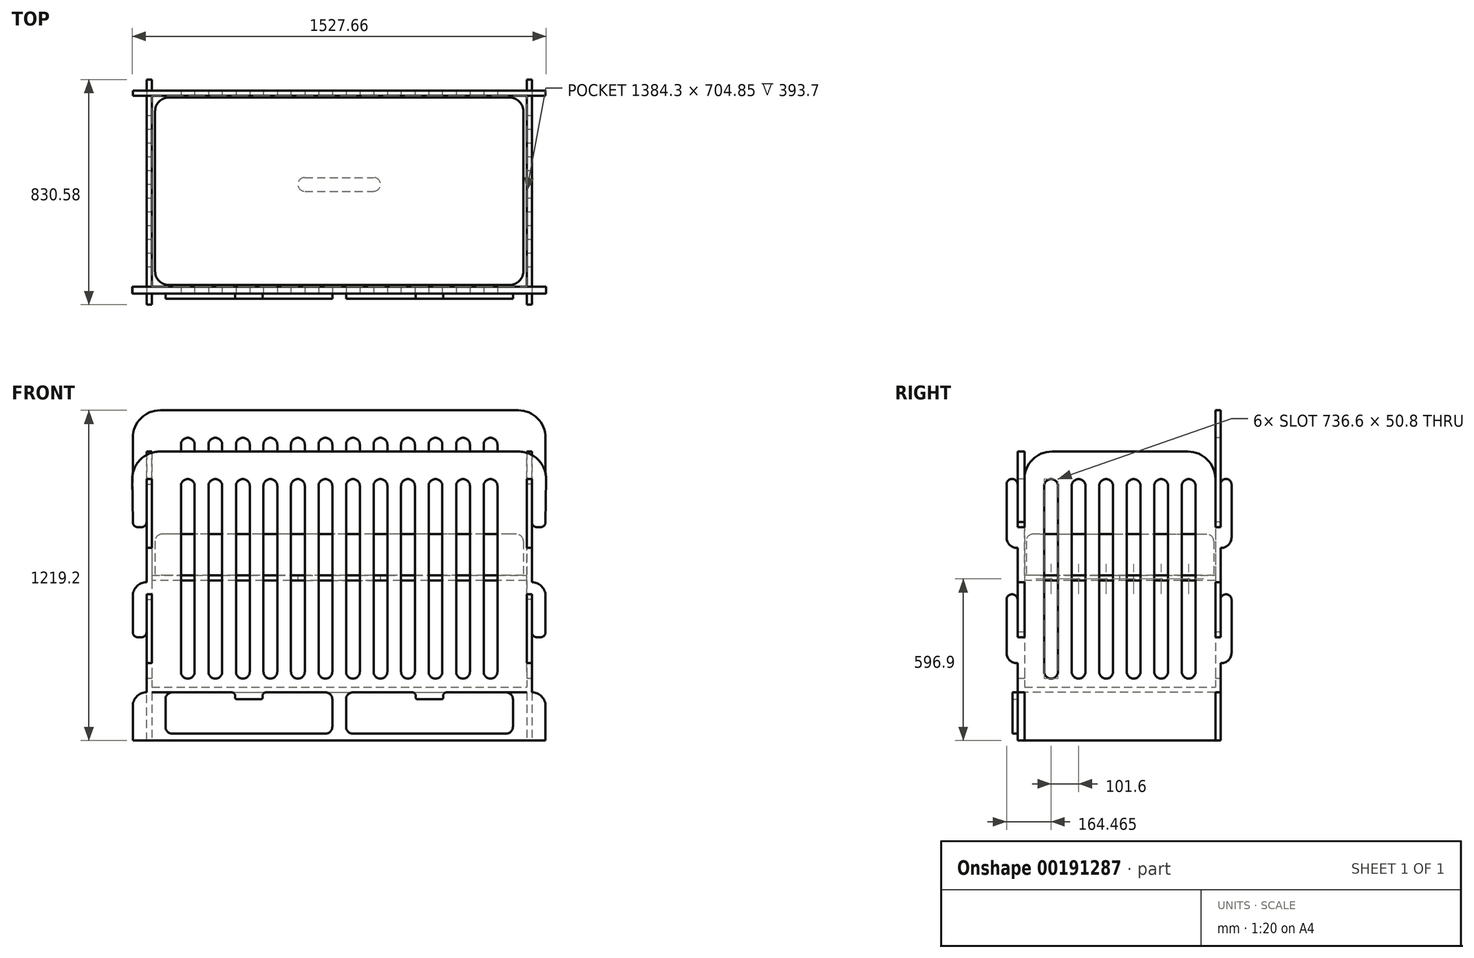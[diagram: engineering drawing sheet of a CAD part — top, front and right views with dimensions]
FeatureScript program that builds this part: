
annotation { "Feature Type Name" : "Feature", "Feature Type Description" : "" }
export const myFeature = defineFeature(function(context is Context, id is Id, definition is map)
    precondition{}
    {
        {
            var Q0;
            Q0=qCreatedBy(makeId("Front.planeOp"),FACE);
            var sketch = newSketch(context, id + "F0", { "sketchPlane" : qUnion([Q0])});
            skLineSegment(sketch, "E0", {"start": v(0, 360.7) * mm, "end": v(0, -747.32) * mm, "construction": true});
            skLineSegment(sketch, "E1", {"start": v(-1058.75, 0) * mm, "end": v(1231.14, 0) * mm, "construction": true});
            skLineSegment(sketch, "E2.bottom", {"start": v(-660.4, 304.8) * mm, "end": v(660.4, 304.8) * mm});
            skLineSegment(sketch, "E2.top", {"start": v(-762, -914.4) * mm, "end": v(762, -914.4) * mm});
            skLineSegment(sketch, "E2.left", {"start": v(-762, 203.2) * mm, "end": v(-762, -914.4) * mm});
            skLineSegment(sketch, "E2.right", {"start": v(762, 203.2) * mm, "end": v(762, -914.4) * mm});
            skPoint(sketch, "E3.visualSharp", {"position": v(-762, 304.8) * mm});
            skArc(sketch, "E3.filletArc", {"start": v(-660.4, 304.8) * mm, "mid": v(-732.24, 275.04) * mm, "end": v(-762, 203.2) * mm});
            skPoint(sketch, "E4.visualSharp", {"position": v(762, 304.8) * mm});
            skArc(sketch, "E4.filletArc", {"start": v(762, 203.2) * mm, "mid": v(732.24, 275.04) * mm, "end": v(660.4, 304.8) * mm});
            skSolve(sketch);
        }
        {
            var Q0;
            Q0 = qSketchRegion(id + "F0", true);
            extrude(context, id + "F1", {"entities" : qUnion([Q0]), "depth" : 19.05 * mm});
        }
        {
            var Q0;
            Q0=makeQuery(id+"F1.opExtrude","CAP_FACE",FACE,{"disambiguationData":[OSD([sQuery(id+"F0.wireOp",EDGE,"E2.bottom"),sQuery(id+"F0.wireOp",EDGE,"E2.top"),sQuery(id+"F0.wireOp",EDGE,"E2.left"),sQuery(id+"F0.wireOp",EDGE,"E2.right"),sQuery(id+"F0.wireOp",EDGE,"E3.filletArc"),sQuery(id+"F0.wireOp",EDGE,"E4.filletArc")])],"isStart":false});
            var sketch = newSketch(context, id + "F2", { "sketchPlane" : qUnion([Q0])});
            skLineSegment(sketch, "E5", {"start": v(-1021.81, 0) * mm, "end": v(1180, 0) * mm, "construction": true});
            skLineSegment(sketch, "E6", {"start": v(0, 448.77) * mm, "end": v(0, -914.4) * mm, "construction": true});
            skLineSegment(sketch, "E7", {"start": v(-742.95, -127) * mm, "end": v(-730.25, -127) * mm});
            skLineSegment(sketch, "E8", {"start": v(-711.2, -107.95) * mm, "end": v(-711.2, -50.8) * mm});
            skLineSegment(sketch, "E9", {"start": v(-711.2, -50.8) * mm, "end": v(-692.15, -50.8) * mm});
            skLineSegment(sketch, "E10", {"start": v(-692.15, -50.8) * mm, "end": v(-692.15, -330.2) * mm});
            skLineSegment(sketch, "E11", {"start": v(-762, -50.8) * mm, "end": v(-762, -107.95) * mm});
            skArc(sketch, "E12.filletArc", {"start": v(-762, -107.95) * mm, "mid": v(-756.42, -121.42) * mm, "end": v(-742.95, -127) * mm});
            skPoint(sketch, "E13.visualSharp", {"position": v(-762, -330.2) * mm});
            skPoint(sketch, "E14.visualSharp", {"position": v(-711.2, -127) * mm});
            skArc(sketch, "E14.filletArc", {"start": v(-730.25, -127) * mm, "mid": v(-716.78, -121.42) * mm, "end": v(-711.2, -107.95) * mm});
            skLineSegment(sketch, "E15", {"start": v(-762, -50.8) * mm, "end": v(-838.2, -50.8) * mm});
            skLineSegment(sketch, "E16", {"start": v(-838.2, -50.8) * mm, "end": v(-838.2, -431.8) * mm});
            skLineSegment(sketch, "E17", {"start": v(-838.2, -431.8) * mm, "end": v(-762, -431.8) * mm});
            skLineSegment(sketch, "E18", {"start": v(-692.15, -330.2) * mm, "end": v(-711.2, -330.2) * mm});
            skLineSegment(sketch, "E19", {"start": v(-762, -381) * mm, "end": v(-762, -431.8) * mm});
            skArc(sketch, "E20.filletArc", {"start": v(-711.2, -330.2) * mm, "mid": v(-747.12, -345.08) * mm, "end": v(-762, -381) * mm});
            skLineSegment(sketch, "E21.0.1.0", {"start": v(-711.2, -514.35) * mm, "end": v(-711.2, -457.2) * mm});
            skLineSegment(sketch, "E21.0.1.1", {"start": v(-838.2, -838.2) * mm, "end": v(-762, -838.2) * mm});
            skPoint(sketch, "E21.0.1.2", {"position": v(-762, -736.6) * mm});
            skArc(sketch, "E21.0.1.3", {"start": v(-711.2, -736.6) * mm, "mid": v(-747.12, -751.48) * mm, "end": v(-762, -787.4) * mm});
            skLineSegment(sketch, "E21.0.1.4", {"start": v(-762, -457.2) * mm, "end": v(-838.2, -457.2) * mm});
            skLineSegment(sketch, "E21.0.1.5", {"start": v(-762, -787.4) * mm, "end": v(-762, -838.2) * mm});
            skLineSegment(sketch, "E21.0.1.6", {"start": v(-692.15, -457.2) * mm, "end": v(-692.15, -736.6) * mm});
            skLineSegment(sketch, "E21.0.1.7", {"start": v(-838.2, -457.2) * mm, "end": v(-838.2, -838.2) * mm});
            skLineSegment(sketch, "E21.0.1.8", {"start": v(-762, -457.2) * mm, "end": v(-762, -514.35) * mm});
            skPoint(sketch, "E21.0.1.9", {"position": v(-711.2, -533.4) * mm});
            skPoint(sketch, "E21.0.1.10", {"position": v(-762, -736.6) * mm});
            skLineSegment(sketch, "E21.0.1.11", {"start": v(-711.2, -457.2) * mm, "end": v(-692.15, -457.2) * mm});
            skArc(sketch, "E21.0.1.12", {"start": v(-762, -514.35) * mm, "mid": v(-756.42, -527.82) * mm, "end": v(-742.95, -533.4) * mm});
            skLineSegment(sketch, "E21.0.1.13", {"start": v(-742.95, -533.4) * mm, "end": v(-730.25, -533.4) * mm});
            skLineSegment(sketch, "E21.0.1.14", {"start": v(-692.15, -736.6) * mm, "end": v(-711.2, -736.6) * mm});
            skArc(sketch, "E21.0.1.15", {"start": v(-730.25, -533.4) * mm, "mid": v(-716.78, -527.82) * mm, "end": v(-711.2, -514.35) * mm});
            skLineSegment(sketch, "E21.direction1", {"start": v(-838.2, -431.8) * mm, "end": v(-812.8, -431.8) * mm, "construction": true});
            skLineSegment(sketch, "E21.direction2", {"start": v(-838.2, -431.8) * mm, "end": v(-838.2, -838.2) * mm, "construction": true});
            skLineSegment(sketch, "E22.MirrorCS", {"start": v(742.95, -127) * mm, "end": v(730.25, -127) * mm});
            skLineSegment(sketch, "E23.MirrorCS", {"start": v(692.15, -330.2) * mm, "end": v(711.2, -330.2) * mm});
            skArc(sketch, "E24.MirrorCS", {"start": v(762, -107.95) * mm, "mid": v(756.42, -121.42) * mm, "end": v(742.95, -127) * mm});
            skLineSegment(sketch, "E25.MirrorCS", {"start": v(692.15, -736.6) * mm, "end": v(711.2, -736.6) * mm});
            skLineSegment(sketch, "E26.MirrorCS", {"start": v(711.2, -50.8) * mm, "end": v(692.15, -50.8) * mm});
            skArc(sketch, "E27.MirrorCS", {"start": v(730.25, -127) * mm, "mid": v(716.78, -121.42) * mm, "end": v(711.2, -107.95) * mm});
            skLineSegment(sketch, "E28.MirrorCS", {"start": v(742.95, -533.4) * mm, "end": v(730.25, -533.4) * mm});
            skArc(sketch, "E29.MirrorCS", {"start": v(762, -514.35) * mm, "mid": v(756.42, -527.82) * mm, "end": v(742.95, -533.4) * mm});
            skLineSegment(sketch, "E30.MirrorCS", {"start": v(711.2, -457.2) * mm, "end": v(692.15, -457.2) * mm});
            skArc(sketch, "E31.MirrorCS", {"start": v(730.25, -533.4) * mm, "mid": v(716.78, -527.82) * mm, "end": v(711.2, -514.35) * mm});
            skLineSegment(sketch, "E32.MirrorCS", {"start": v(838.2, -457.2) * mm, "end": v(838.2, -838.2) * mm});
            skLineSegment(sketch, "E33.MirrorCS", {"start": v(838.2, -431.8) * mm, "end": v(838.2, -838.2) * mm, "construction": true});
            skLineSegment(sketch, "E34.MirrorCS", {"start": v(838.2, -431.8) * mm, "end": v(812.8, -431.8) * mm, "construction": true});
            skPoint(sketch, "E35.MirrorP", {"position": v(762, -736.6) * mm});
            skPoint(sketch, "E36.MirrorP", {"position": v(762, -330.2) * mm});
            skLineSegment(sketch, "E37.MirrorCS", {"start": v(711.2, -107.95) * mm, "end": v(711.2, -50.8) * mm});
            skLineSegment(sketch, "E38.MirrorCS", {"start": v(692.15, -50.8) * mm, "end": v(692.15, -330.2) * mm});
            skLineSegment(sketch, "E39.MirrorCS", {"start": v(762, -50.8) * mm, "end": v(762, -107.95) * mm});
            skLineSegment(sketch, "E40.MirrorCS", {"start": v(762, -787.4) * mm, "end": v(762, -838.2) * mm});
            skLineSegment(sketch, "E41.MirrorCS", {"start": v(762, -457.2) * mm, "end": v(838.2, -457.2) * mm});
            skPoint(sketch, "E42.MirrorP", {"position": v(711.2, -533.4) * mm});
            skLineSegment(sketch, "E43.MirrorCS", {"start": v(838.2, -431.8) * mm, "end": v(762, -431.8) * mm});
            skLineSegment(sketch, "E44.MirrorCS", {"start": v(762, -50.8) * mm, "end": v(838.2, -50.8) * mm});
            skLineSegment(sketch, "E45.MirrorCS", {"start": v(762, -457.2) * mm, "end": v(762, -514.35) * mm});
            skLineSegment(sketch, "E46.MirrorCS", {"start": v(838.2, -50.8) * mm, "end": v(838.2, -431.8) * mm});
            skLineSegment(sketch, "E47.MirrorCS", {"start": v(711.2, -514.35) * mm, "end": v(711.2, -457.2) * mm});
            skArc(sketch, "E48.MirrorCS", {"start": v(711.2, -330.2) * mm, "mid": v(747.12, -345.08) * mm, "end": v(762, -381) * mm});
            skLineSegment(sketch, "E49.MirrorCS", {"start": v(762, -381) * mm, "end": v(762, -431.8) * mm});
            skArc(sketch, "E50.MirrorCS", {"start": v(711.2, -736.6) * mm, "mid": v(747.12, -751.48) * mm, "end": v(762, -787.4) * mm});
            skPoint(sketch, "E51.MirrorP", {"position": v(711.2, -127) * mm});
            skLineSegment(sketch, "E52.MirrorCS", {"start": v(838.2, -838.2) * mm, "end": v(762, -838.2) * mm});
            skLineSegment(sketch, "E53.MirrorCS", {"start": v(692.15, -457.2) * mm, "end": v(692.15, -736.6) * mm});
            skSolve(sketch);
        }
        {
            var Q0;
            Q0 = qSketchRegion(id + "F2", true);
            extrude(context, id + "F3", {"entities" : qUnion([Q0]), "operationType" : NewBodyOperationType.REMOVE, "endBound" : BoundingType.THROUGH_ALL, "oppositeDirection" : true, "depth" : 25.4 * mm});
        }
        {
            var Q0;
            Q0=makeQuery(id+"F1.opExtrude","CAP_FACE",FACE,{"disambiguationData":[OSD([sQuery(id+"F0.wireOp",EDGE,"E2.bottom"),sQuery(id+"F0.wireOp",EDGE,"E2.top"),sQuery(id+"F0.wireOp",EDGE,"E2.left"),sQuery(id+"F0.wireOp",EDGE,"E2.right"),sQuery(id+"F0.wireOp",EDGE,"E3.filletArc"),sQuery(id+"F0.wireOp",EDGE,"E4.filletArc")])],"isStart":false});
            var sketch = newSketch(context, id + "F4", { "sketchPlane" : qUnion([Q0])});
            skLineSegment(sketch, "E54", {"start": v(0, 304.8) * mm, "end": v(0, -914.4) * mm, "construction": true});
            skLineSegment(sketch, "E55", {"start": v(-762, 0) * mm, "end": v(762, 0) * mm, "construction": true});
            skLineSegment(sketch, "E56.bottom", {"start": v(-50.8, 203.2) * mm, "end": v(-50.8, 203.2) * mm});
            skLineSegment(sketch, "E56.top", {"start": v(-50.8, -685.8) * mm, "end": v(-50.8, -685.8) * mm});
            skLineSegment(sketch, "E56.left", {"start": v(-76.2, 177.8) * mm, "end": v(-76.2, -660.4) * mm});
            skLineSegment(sketch, "E56.right", {"start": v(-25.4, 177.8) * mm, "end": v(-25.4, -660.4) * mm});
            skLineSegment(sketch, "E57", {"start": v(-762, -787.4) * mm, "end": v(762, -787.4) * mm, "construction": true});
            skPoint(sketch, "E58.visualSharp", {"position": v(-76.2, 203.2) * mm});
            skArc(sketch, "E58.filletArc", {"start": v(-50.8, 203.2) * mm, "mid": v(-68.76, 195.76) * mm, "end": v(-76.2, 177.8) * mm});
            skPoint(sketch, "E59.visualSharp", {"position": v(-25.4, 203.2) * mm});
            skArc(sketch, "E59.filletArc", {"start": v(-25.4, 177.8) * mm, "mid": v(-32.84, 195.76) * mm, "end": v(-50.8, 203.2) * mm});
            skPoint(sketch, "E60.visualSharp", {"position": v(-76.2, -685.8) * mm});
            skArc(sketch, "E60.filletArc", {"start": v(-76.2, -660.4) * mm, "mid": v(-68.76, -678.36) * mm, "end": v(-50.8, -685.8) * mm});
            skPoint(sketch, "E61.visualSharp", {"position": v(-25.4, -685.8) * mm});
            skArc(sketch, "E61.filletArc", {"start": v(-50.8, -685.8) * mm, "mid": v(-32.84, -678.36) * mm, "end": v(-25.4, -660.4) * mm});
            skLineSegment(sketch, "E62.1.0.0", {"start": v(-177.8, 177.8) * mm, "end": v(-177.8, -660.4) * mm});
            skLineSegment(sketch, "E62.1.0.1", {"start": v(-127, 177.8) * mm, "end": v(-127, -660.4) * mm});
            skPoint(sketch, "E62.1.0.2", {"position": v(-127, -685.8) * mm});
            skPoint(sketch, "E62.1.0.3", {"position": v(-177.8, -685.8) * mm});
            skPoint(sketch, "E62.1.0.4", {"position": v(-127, 203.2) * mm});
            skPoint(sketch, "E62.1.0.5", {"position": v(-177.8, 203.2) * mm});
            skArc(sketch, "E62.1.0.6", {"start": v(-127, 177.8) * mm, "mid": v(-134.44, 195.76) * mm, "end": v(-152.4, 203.2) * mm});
            skArc(sketch, "E62.1.0.7", {"start": v(-177.8, -660.4) * mm, "mid": v(-170.36, -678.36) * mm, "end": v(-152.4, -685.8) * mm});
            skArc(sketch, "E62.1.0.8", {"start": v(-152.4, -685.8) * mm, "mid": v(-134.44, -678.36) * mm, "end": v(-127, -660.4) * mm});
            skArc(sketch, "E62.1.0.9", {"start": v(-152.4, 203.2) * mm, "mid": v(-170.36, 195.76) * mm, "end": v(-177.8, 177.8) * mm});
            skLineSegment(sketch, "E62.2.0.0", {"start": v(-279.4, 177.8) * mm, "end": v(-279.4, -660.4) * mm});
            skLineSegment(sketch, "E62.2.0.1", {"start": v(-228.6, 177.8) * mm, "end": v(-228.6, -660.4) * mm});
            skPoint(sketch, "E62.2.0.2", {"position": v(-228.6, -685.8) * mm});
            skPoint(sketch, "E62.2.0.3", {"position": v(-279.4, -685.8) * mm});
            skPoint(sketch, "E62.2.0.4", {"position": v(-228.6, 203.2) * mm});
            skPoint(sketch, "E62.2.0.5", {"position": v(-279.4, 203.2) * mm});
            skArc(sketch, "E62.2.0.6", {"start": v(-228.6, 177.8) * mm, "mid": v(-236.04, 195.76) * mm, "end": v(-254, 203.2) * mm});
            skArc(sketch, "E62.2.0.7", {"start": v(-279.4, -660.4) * mm, "mid": v(-271.96, -678.36) * mm, "end": v(-254, -685.8) * mm});
            skArc(sketch, "E62.2.0.8", {"start": v(-254, -685.8) * mm, "mid": v(-236.04, -678.36) * mm, "end": v(-228.6, -660.4) * mm});
            skArc(sketch, "E62.2.0.9", {"start": v(-254, 203.2) * mm, "mid": v(-271.96, 195.76) * mm, "end": v(-279.4, 177.8) * mm});
            skLineSegment(sketch, "E62.3.0.0", {"start": v(-381, 177.8) * mm, "end": v(-381, -660.4) * mm});
            skLineSegment(sketch, "E62.3.0.1", {"start": v(-330.2, 177.8) * mm, "end": v(-330.2, -660.4) * mm});
            skPoint(sketch, "E62.3.0.2", {"position": v(-330.2, -685.8) * mm});
            skPoint(sketch, "E62.3.0.3", {"position": v(-381, -685.8) * mm});
            skPoint(sketch, "E62.3.0.4", {"position": v(-330.2, 203.2) * mm});
            skPoint(sketch, "E62.3.0.5", {"position": v(-381, 203.2) * mm});
            skArc(sketch, "E62.3.0.6", {"start": v(-330.2, 177.8) * mm, "mid": v(-337.64, 195.76) * mm, "end": v(-355.6, 203.2) * mm});
            skArc(sketch, "E62.3.0.7", {"start": v(-381, -660.4) * mm, "mid": v(-373.56, -678.36) * mm, "end": v(-355.6, -685.8) * mm});
            skArc(sketch, "E62.3.0.8", {"start": v(-355.6, -685.8) * mm, "mid": v(-337.64, -678.36) * mm, "end": v(-330.2, -660.4) * mm});
            skArc(sketch, "E62.3.0.9", {"start": v(-355.6, 203.2) * mm, "mid": v(-373.56, 195.76) * mm, "end": v(-381, 177.8) * mm});
            skLineSegment(sketch, "E62.4.0.0", {"start": v(-482.6, 177.8) * mm, "end": v(-482.6, -660.4) * mm});
            skLineSegment(sketch, "E62.4.0.1", {"start": v(-431.8, 177.8) * mm, "end": v(-431.8, -660.4) * mm});
            skPoint(sketch, "E62.4.0.2", {"position": v(-431.8, -685.8) * mm});
            skPoint(sketch, "E62.4.0.3", {"position": v(-482.6, -685.8) * mm});
            skPoint(sketch, "E62.4.0.4", {"position": v(-431.8, 203.2) * mm});
            skPoint(sketch, "E62.4.0.5", {"position": v(-482.6, 203.2) * mm});
            skArc(sketch, "E62.4.0.6", {"start": v(-431.8, 177.8) * mm, "mid": v(-439.24, 195.76) * mm, "end": v(-457.2, 203.2) * mm});
            skArc(sketch, "E62.4.0.7", {"start": v(-482.6, -660.4) * mm, "mid": v(-475.16, -678.36) * mm, "end": v(-457.2, -685.8) * mm});
            skArc(sketch, "E62.4.0.8", {"start": v(-457.2, -685.8) * mm, "mid": v(-439.24, -678.36) * mm, "end": v(-431.8, -660.4) * mm});
            skArc(sketch, "E62.4.0.9", {"start": v(-457.2, 203.2) * mm, "mid": v(-475.16, 195.76) * mm, "end": v(-482.6, 177.8) * mm});
            skLineSegment(sketch, "E62.5.0.0", {"start": v(-584.2, 177.8) * mm, "end": v(-584.2, -660.4) * mm});
            skLineSegment(sketch, "E62.5.0.1", {"start": v(-533.4, 177.8) * mm, "end": v(-533.4, -660.4) * mm});
            skPoint(sketch, "E62.5.0.2", {"position": v(-533.4, -685.8) * mm});
            skPoint(sketch, "E62.5.0.3", {"position": v(-584.2, -685.8) * mm});
            skPoint(sketch, "E62.5.0.4", {"position": v(-533.4, 203.2) * mm});
            skPoint(sketch, "E62.5.0.5", {"position": v(-584.2, 203.2) * mm});
            skArc(sketch, "E62.5.0.6", {"start": v(-533.4, 177.8) * mm, "mid": v(-540.84, 195.76) * mm, "end": v(-558.8, 203.2) * mm});
            skArc(sketch, "E62.5.0.7", {"start": v(-584.2, -660.4) * mm, "mid": v(-576.76, -678.36) * mm, "end": v(-558.8, -685.8) * mm});
            skArc(sketch, "E62.5.0.8", {"start": v(-558.8, -685.8) * mm, "mid": v(-540.84, -678.36) * mm, "end": v(-533.4, -660.4) * mm});
            skArc(sketch, "E62.5.0.9", {"start": v(-558.8, 203.2) * mm, "mid": v(-576.76, 195.76) * mm, "end": v(-584.2, 177.8) * mm});
            skLineSegment(sketch, "E62.direction1", {"start": v(-76.2, -685.8) * mm, "end": v(-177.8, -685.8) * mm, "construction": true});
            skLineSegment(sketch, "E63.MirrorCS", {"start": v(76.2, -685.8) * mm, "end": v(177.8, -685.8) * mm, "construction": true});
            skArc(sketch, "E64.MirrorCS", {"start": v(152.4, -685.8) * mm, "mid": v(134.44, -678.36) * mm, "end": v(127, -660.4) * mm});
            skArc(sketch, "E65.MirrorCS", {"start": v(457.2, 203.2) * mm, "mid": v(475.16, 195.76) * mm, "end": v(482.6, 177.8) * mm});
            skArc(sketch, "E66.MirrorCS", {"start": v(152.4, 203.2) * mm, "mid": v(170.36, 195.76) * mm, "end": v(177.8, 177.8) * mm});
            skArc(sketch, "E67.MirrorCS", {"start": v(279.4, -660.4) * mm, "mid": v(271.96, -678.36) * mm, "end": v(254, -685.8) * mm});
            skArc(sketch, "E68.MirrorCS", {"start": v(431.8, 177.8) * mm, "mid": v(439.24, 195.76) * mm, "end": v(457.2, 203.2) * mm});
            skArc(sketch, "E69.MirrorCS", {"start": v(533.4, 177.8) * mm, "mid": v(540.84, 195.76) * mm, "end": v(558.8, 203.2) * mm});
            skArc(sketch, "E70.MirrorCS", {"start": v(254, -685.8) * mm, "mid": v(236.04, -678.36) * mm, "end": v(228.6, -660.4) * mm});
            skArc(sketch, "E71.MirrorCS", {"start": v(584.2, -660.4) * mm, "mid": v(576.76, -678.36) * mm, "end": v(558.8, -685.8) * mm});
            skArc(sketch, "E72.MirrorCS", {"start": v(254, 203.2) * mm, "mid": v(271.96, 195.76) * mm, "end": v(279.4, 177.8) * mm});
            skArc(sketch, "E73.MirrorCS", {"start": v(330.2, 177.8) * mm, "mid": v(337.64, 195.76) * mm, "end": v(355.6, 203.2) * mm});
            skArc(sketch, "E74.MirrorCS", {"start": v(482.6, -660.4) * mm, "mid": v(475.16, -678.36) * mm, "end": v(457.2, -685.8) * mm});
            skArc(sketch, "E75.MirrorCS", {"start": v(177.8, -660.4) * mm, "mid": v(170.36, -678.36) * mm, "end": v(152.4, -685.8) * mm});
            skArc(sketch, "E76.MirrorCS", {"start": v(381, -660.4) * mm, "mid": v(373.56, -678.36) * mm, "end": v(355.6, -685.8) * mm});
            skArc(sketch, "E77.MirrorCS", {"start": v(355.6, -685.8) * mm, "mid": v(337.64, -678.36) * mm, "end": v(330.2, -660.4) * mm});
            skArc(sketch, "E78.MirrorCS", {"start": v(127, 177.8) * mm, "mid": v(134.44, 195.76) * mm, "end": v(152.4, 203.2) * mm});
            skArc(sketch, "E79.MirrorCS", {"start": v(50.8, -685.8) * mm, "mid": v(32.84, -678.36) * mm, "end": v(25.4, -660.4) * mm});
            skArc(sketch, "E80.MirrorCS", {"start": v(457.2, -685.8) * mm, "mid": v(439.24, -678.36) * mm, "end": v(431.8, -660.4) * mm});
            skArc(sketch, "E81.MirrorCS", {"start": v(558.8, 203.2) * mm, "mid": v(576.76, 195.76) * mm, "end": v(584.2, 177.8) * mm});
            skArc(sketch, "E82.MirrorCS", {"start": v(558.8, -685.8) * mm, "mid": v(540.84, -678.36) * mm, "end": v(533.4, -660.4) * mm});
            skArc(sketch, "E83.MirrorCS", {"start": v(76.2, -660.4) * mm, "mid": v(68.76, -678.36) * mm, "end": v(50.8, -685.8) * mm});
            skArc(sketch, "E84.MirrorCS", {"start": v(25.4, 177.8) * mm, "mid": v(32.84, 195.76) * mm, "end": v(50.8, 203.2) * mm});
            skArc(sketch, "E85.MirrorCS", {"start": v(355.6, 203.2) * mm, "mid": v(373.56, 195.76) * mm, "end": v(381, 177.8) * mm});
            skArc(sketch, "E86.MirrorCS", {"start": v(228.6, 177.8) * mm, "mid": v(236.04, 195.76) * mm, "end": v(254, 203.2) * mm});
            skArc(sketch, "E87.MirrorCS", {"start": v(50.8, 203.2) * mm, "mid": v(68.76, 195.76) * mm, "end": v(76.2, 177.8) * mm});
            skPoint(sketch, "E88.MirrorP", {"position": v(76.2, 203.2) * mm});
            skPoint(sketch, "E89.MirrorP", {"position": v(381, 203.2) * mm});
            skPoint(sketch, "E90.MirrorP", {"position": v(177.8, 203.2) * mm});
            skLineSegment(sketch, "E91.MirrorCS", {"start": v(533.4, 177.8) * mm, "end": v(533.4, -660.4) * mm});
            skPoint(sketch, "E92.MirrorP", {"position": v(228.6, 203.2) * mm});
            skPoint(sketch, "E93.MirrorP", {"position": v(584.2, 203.2) * mm});
            skPoint(sketch, "E94.MirrorP", {"position": v(431.8, 203.2) * mm});
            skPoint(sketch, "E95.MirrorP", {"position": v(482.6, 203.2) * mm});
            skPoint(sketch, "E96.MirrorP", {"position": v(279.4, 203.2) * mm});
            skLineSegment(sketch, "E97.MirrorCS", {"start": v(482.6, 177.8) * mm, "end": v(482.6, -660.4) * mm});
            skPoint(sketch, "E98.MirrorP", {"position": v(76.2, -685.8) * mm});
            skLineSegment(sketch, "E99.MirrorCS", {"start": v(279.4, 177.8) * mm, "end": v(279.4, -660.4) * mm});
            skLineSegment(sketch, "E100.MirrorCS", {"start": v(228.6, 177.8) * mm, "end": v(228.6, -660.4) * mm});
            skLineSegment(sketch, "E101.MirrorCS", {"start": v(76.2, 177.8) * mm, "end": v(76.2, -660.4) * mm});
            skPoint(sketch, "E102.MirrorP", {"position": v(127, 203.2) * mm});
            skLineSegment(sketch, "E103.MirrorCS", {"start": v(25.4, 177.8) * mm, "end": v(25.4, -660.4) * mm});
            skPoint(sketch, "E104.MirrorP", {"position": v(25.4, -685.8) * mm});
            skPoint(sketch, "E105.MirrorP", {"position": v(533.4, -685.8) * mm});
            skLineSegment(sketch, "E106.MirrorCS", {"start": v(381, 177.8) * mm, "end": v(381, -660.4) * mm});
            skPoint(sketch, "E107.MirrorP", {"position": v(330.2, -685.8) * mm});
            skPoint(sketch, "E108.MirrorP", {"position": v(127, -685.8) * mm});
            skPoint(sketch, "E109.MirrorP", {"position": v(431.8, -685.8) * mm});
            skPoint(sketch, "E110.MirrorP", {"position": v(228.6, -685.8) * mm});
            skLineSegment(sketch, "E111.MirrorCS", {"start": v(431.8, 177.8) * mm, "end": v(431.8, -660.4) * mm});
            skPoint(sketch, "E112.MirrorP", {"position": v(381, -685.8) * mm});
            skPoint(sketch, "E113.MirrorP", {"position": v(177.8, -685.8) * mm});
            skLineSegment(sketch, "E114.MirrorCS", {"start": v(330.2, 177.8) * mm, "end": v(330.2, -660.4) * mm});
            skLineSegment(sketch, "E115.MirrorCS", {"start": v(127, 177.8) * mm, "end": v(127, -660.4) * mm});
            skPoint(sketch, "E116.MirrorP", {"position": v(25.4, 203.2) * mm});
            skLineSegment(sketch, "E117.MirrorCS", {"start": v(177.8, 177.8) * mm, "end": v(177.8, -660.4) * mm});
            skPoint(sketch, "E118.MirrorP", {"position": v(330.2, 203.2) * mm});
            skPoint(sketch, "E119.MirrorP", {"position": v(482.6, -685.8) * mm});
            skPoint(sketch, "E120.MirrorP", {"position": v(584.2, -685.8) * mm});
            skPoint(sketch, "E121.MirrorP", {"position": v(533.4, 203.2) * mm});
            skLineSegment(sketch, "E122.MirrorCS", {"start": v(584.2, 177.8) * mm, "end": v(584.2, -660.4) * mm});
            skPoint(sketch, "E123.MirrorP", {"position": v(279.4, -685.8) * mm});
            skSolve(sketch);
        }
        {
            var Q0;
            Q0 = qSketchRegion(id + "F4", true);
            extrude(context, id + "F5", {"entities" : qUnion([Q0]), "operationType" : NewBodyOperationType.REMOVE, "endBound" : BoundingType.THROUGH_ALL, "oppositeDirection" : true, "depth" : 25.4 * mm});
        }
        {
            var Q0;
            Q0=makeQuery(id+"F3.boolean.opBoolean","COPY",FACE,{"derivedFrom":makeQuery(id+"F3.opExtrude","SWEPT_FACE",FACE,{"disambiguationData":[OSD([sQuery(id+"F2.wireOp",EDGE,"E10")])]})});
            var sketch = newSketch(context, id + "F6", { "sketchPlane" : qUnion([Q0])});
            skPoint(sketch, "E124.0", {"position": v(0, -914.4) * mm});
            skLineSegment(sketch, "E125.bottom", {"start": v(0, -914.4) * mm, "end": v(749.3, -914.4) * mm});
            skLineSegment(sketch, "E125.top", {"start": v(0, 0) * mm, "end": v(749.3, 0) * mm});
            skLineSegment(sketch, "E126", {"start": v(0, 0) * mm, "end": v(0, 31.75) * mm});
            skLineSegment(sketch, "E127", {"start": v(-19.05, 50.8) * mm, "end": v(-21.6, 50.8) * mm});
            skLineSegment(sketch, "E128", {"start": v(-40.64, 31.75) * mm, "end": v(-40.64, -165.1) * mm});
            skLineSegment(sketch, "E129", {"start": v(-2.54, -203.2) * mm, "end": v(0, -203.2) * mm});
            skPoint(sketch, "E129.endSnap0", {"position": v(0, -190.5) * mm});
            skLineSegment(sketch, "E130.trimOffspring", {"start": v(0, -50.8) * mm, "end": v(0, 0) * mm});
            skPoint(sketch, "E131.0", {"position": v(0, -457.2) * mm});
            skLineSegment(sketch, "E132", {"start": v(0, -457.2) * mm, "end": v(0, -393.94) * mm});
            skLineSegment(sketch, "E133", {"start": v(-19.05, -374.9) * mm, "end": v(-21.6, -374.9) * mm});
            skLineSegment(sketch, "E134", {"start": v(-40.64, -393.94) * mm, "end": v(-40.64, -590.8) * mm});
            skLineSegment(sketch, "E135", {"start": v(-2.54, -628.9) * mm, "end": v(0, -628.9) * mm});
            skPoint(sketch, "E136.visualSharp", {"position": v(0, 50.8) * mm});
            skArc(sketch, "E136.filletArc", {"start": v(0, 31.75) * mm, "mid": v(-5.58, 45.22) * mm, "end": v(-19.05, 50.8) * mm});
            skPoint(sketch, "E137.visualSharp", {"position": v(-40.64, 50.8) * mm});
            skArc(sketch, "E137.filletArc", {"start": v(-21.6, 50.8) * mm, "mid": v(-35.06, 45.22) * mm, "end": v(-40.64, 31.75) * mm});
            skPoint(sketch, "E138.visualSharp", {"position": v(-40.64, -203.2) * mm});
            skArc(sketch, "E138.filletArc", {"start": v(-40.64, -165.1) * mm, "mid": v(-29.48, -192.04) * mm, "end": v(-2.54, -203.2) * mm});
            skArc(sketch, "E139.filletArc", {"start": v(0, -393.94) * mm, "mid": v(-5.58, -380.47) * mm, "end": v(-19.05, -374.9) * mm});
            skPoint(sketch, "E140.visualSharp", {"position": v(-40.64, -374.9) * mm});
            skArc(sketch, "E140.filletArc", {"start": v(-21.6, -374.9) * mm, "mid": v(-35.06, -380.47) * mm, "end": v(-40.64, -393.94) * mm});
            skLineSegment(sketch, "E141", {"start": v(0, -393.94) * mm, "end": v(0, -203.2) * mm});
            skPoint(sketch, "E142.visualSharp", {"position": v(-40.64, -628.9) * mm});
            skArc(sketch, "E142.filletArc", {"start": v(-40.64, -590.8) * mm, "mid": v(-29.48, -617.73) * mm, "end": v(-2.54, -628.9) * mm});
            skLineSegment(sketch, "E143", {"start": v(0, -914.4) * mm, "end": v(0, -628.9) * mm});
            skLineSegment(sketch, "E144", {"start": v(374.65, 0) * mm, "end": v(374.65, -914.4) * mm, "construction": true});
            skLineSegment(sketch, "E145.MirrorCS", {"start": v(751.84, -203.2) * mm, "end": v(749.3, -203.2) * mm});
            skLineSegment(sketch, "E146.MirrorCS", {"start": v(768.35, 50.8) * mm, "end": v(770.89, 50.8) * mm});
            skLineSegment(sketch, "E147.MirrorCS", {"start": v(749.3, 0) * mm, "end": v(749.3, 31.75) * mm});
            skArc(sketch, "E148.MirrorCS", {"start": v(770.89, 50.8) * mm, "mid": v(784.36, 45.22) * mm, "end": v(789.94, 31.75) * mm});
            skArc(sketch, "E149.MirrorCS", {"start": v(749.3, 31.75) * mm, "mid": v(754.88, 45.22) * mm, "end": v(768.35, 50.8) * mm});
            skArc(sketch, "E150.MirrorCS", {"start": v(789.94, -165.1) * mm, "mid": v(778.78, -192.04) * mm, "end": v(751.84, -203.2) * mm});
            skLineSegment(sketch, "E151.MirrorCS", {"start": v(789.94, 31.75) * mm, "end": v(789.94, -165.1) * mm});
            skPoint(sketch, "E152.MirrorP", {"position": v(789.94, 50.8) * mm});
            skPoint(sketch, "E153.MirrorP", {"position": v(789.94, -203.2) * mm});
            skPoint(sketch, "E154.MirrorP", {"position": v(749.3, -190.5) * mm});
            skPoint(sketch, "E155.MirrorP", {"position": v(749.3, 50.8) * mm});
            skLineSegment(sketch, "E156.MirrorCS", {"start": v(751.84, -628.9) * mm, "end": v(749.3, -628.9) * mm});
            skArc(sketch, "E157.MirrorCS", {"start": v(749.3, -393.94) * mm, "mid": v(754.88, -380.47) * mm, "end": v(768.35, -374.9) * mm});
            skArc(sketch, "E158.MirrorCS", {"start": v(770.89, -374.9) * mm, "mid": v(784.36, -380.47) * mm, "end": v(789.94, -393.94) * mm});
            skLineSegment(sketch, "E159.MirrorCS", {"start": v(768.35, -374.9) * mm, "end": v(770.89, -374.9) * mm});
            skArc(sketch, "E160.MirrorCS", {"start": v(789.94, -590.8) * mm, "mid": v(778.78, -617.73) * mm, "end": v(751.84, -628.9) * mm});
            skPoint(sketch, "E161.MirrorP", {"position": v(789.94, -374.9) * mm});
            skLineSegment(sketch, "E162.MirrorCS", {"start": v(789.94, -393.94) * mm, "end": v(789.94, -590.8) * mm});
            skPoint(sketch, "E163.MirrorP", {"position": v(749.3, -457.2) * mm});
            skPoint(sketch, "E164.MirrorP", {"position": v(789.94, -628.9) * mm});
            skPoint(sketch, "E165.MirrorCS.start.orphan", {"position": v(749.3, -50.8) * mm});
            skLineSegment(sketch, "E166.trimOffspring", {"start": v(749.3, -393.94) * mm, "end": v(749.3, -203.2) * mm});
            skLineSegment(sketch, "E167", {"start": v(749.3, -628.9) * mm, "end": v(749.3, -914.4) * mm});
            skSolve(sketch);
        }
        {
            var Q0;
            Q0 = qSketchRegion(id + "F6", true);
            extrude(context, id + "F7", {"entities" : qUnion([Q0]), "operationType" : NewBodyOperationType.ADD, "depth" : 19.05 * mm});
        }
        {
            var Q0;
            Q0=makeQuery(id+"F1.opExtrude","SWEPT_BODY",BODY,{"disambiguationData":[OSD([sQuery(id+"F0.wireOp",EDGE,"E2.bottom"),sQuery(id+"F0.wireOp",EDGE,"E2.top"),sQuery(id+"F0.wireOp",EDGE,"E2.left"),sQuery(id+"F0.wireOp",EDGE,"E2.right"),sQuery(id+"F0.wireOp",EDGE,"E3.filletArc"),sQuery(id+"F0.wireOp",EDGE,"E4.filletArc")])]});
            var Q1;
            Q1=qCreatedBy(makeId("Right.planeOp"),FACE);
            mirror(context, id + "F8", {"operationType" : NewBodyOperationType.ADD, "entities" : qUnion([Q0]), "mirrorPlane" : qUnion([Q1])});
        }
        {
            var Q0;
            Q0=makeQuery(id+"F7.opExtrude","SWEPT_FACE",FACE,{"disambiguationData":[OSD([sQuery(id+"F6.wireOp",EDGE,"E166.trimOffspring")])]});
            var sketch = newSketch(context, id + "F9", { "sketchPlane" : qUnion([Q0])});
            skArc(sketch, "E168.0", {"start": v(-730.25, -127) * mm, "mid": v(-716.78, -121.42) * mm, "end": v(-711.2, -107.95) * mm});
            skLineSegment(sketch, "E169.0", {"start": v(-742.95, -127) * mm, "end": v(-730.25, -127) * mm});
            skArc(sketch, "E170.0", {"start": v(-762, -107.95) * mm, "mid": v(-756.42, -121.42) * mm, "end": v(-742.95, -127) * mm});
            skArc(sketch, "E171.0", {"start": v(-711.2, -330.2) * mm, "mid": v(-747.12, -345.08) * mm, "end": v(-762, -381) * mm});
            skLineSegment(sketch, "E172.0", {"start": v(-762, -381) * mm, "end": v(-762, -514.35) * mm});
            skArc(sketch, "E173.0", {"start": v(-762, -514.35) * mm, "mid": v(-756.42, -527.82) * mm, "end": v(-742.95, -533.4) * mm});
            skLineSegment(sketch, "E174.0", {"start": v(-742.95, -533.4) * mm, "end": v(-730.25, -533.4) * mm});
            skArc(sketch, "E175.0", {"start": v(-730.25, -533.4) * mm, "mid": v(-716.78, -527.82) * mm, "end": v(-711.2, -514.35) * mm});
            skArc(sketch, "E176.0", {"start": v(-711.2, -736.6) * mm, "mid": v(-747.12, -751.48) * mm, "end": v(-762, -787.4) * mm});
            skLineSegment(sketch, "E177.0", {"start": v(-762, -787.4) * mm, "end": v(-762, -914.4) * mm});
            skLineSegment(sketch, "E178.0", {"start": v(-762, -914.4) * mm, "end": v(-711.2, -914.4) * mm});
            skLineSegment(sketch, "E179.0", {"start": v(-711.2, -914.4) * mm, "end": v(-692.15, -914.4) * mm});
            skLineSegment(sketch, "E180.0", {"start": v(-692.15, -914.4) * mm, "end": v(692.15, -914.4) * mm});
            skLineSegment(sketch, "E181.0", {"start": v(711.2, -914.4) * mm, "end": v(692.15, -914.4) * mm});
            skLineSegment(sketch, "E182.0", {"start": v(711.2, -914.4) * mm, "end": v(762, -914.4) * mm});
            skLineSegment(sketch, "E183.0", {"start": v(762, -787.4) * mm, "end": v(762, -914.4) * mm});
            skArc(sketch, "E184.0", {"start": v(711.2, -736.6) * mm, "mid": v(747.12, -751.48) * mm, "end": v(762, -787.4) * mm});
            skArc(sketch, "E185.0", {"start": v(730.25, -533.4) * mm, "mid": v(716.78, -527.82) * mm, "end": v(711.2, -514.35) * mm});
            skLineSegment(sketch, "E186.0", {"start": v(742.95, -533.4) * mm, "end": v(730.25, -533.4) * mm});
            skArc(sketch, "E187.0", {"start": v(762, -514.35) * mm, "mid": v(756.42, -527.82) * mm, "end": v(742.95, -533.4) * mm});
            skLineSegment(sketch, "E188.0", {"start": v(762, -381) * mm, "end": v(762, -514.35) * mm});
            skArc(sketch, "E189.0", {"start": v(711.2, -330.2) * mm, "mid": v(747.12, -345.08) * mm, "end": v(762, -381) * mm});
            skArc(sketch, "E190.0", {"start": v(730.25, -127) * mm, "mid": v(716.78, -121.42) * mm, "end": v(711.2, -107.95) * mm});
            skLineSegment(sketch, "E191.0", {"start": v(742.95, -127) * mm, "end": v(730.25, -127) * mm});
            skArc(sketch, "E192.0", {"start": v(762, -107.95) * mm, "mid": v(756.42, -121.42) * mm, "end": v(742.95, -127) * mm});
            skPoint(sketch, "E193.0.start.orphan", {"position": v(762, 203.2) * mm});
            skPoint(sketch, "E194.0.start.orphan", {"position": v(-762, 203.2) * mm});
            skLineSegment(sketch, "E195", {"start": v(-762, -107.95) * mm, "end": v(-762, 50.8) * mm});
            skLineSegment(sketch, "E196", {"start": v(-660.4, 152.4) * mm, "end": v(662.23, 152.4) * mm});
            skLineSegment(sketch, "E197", {"start": v(763.82, 49.62) * mm, "end": v(762, -107.95) * mm});
            skLineSegment(sketch, "E198", {"start": v(-711.2, -107.95) * mm, "end": v(-711.2, -330.2) * mm});
            skLineSegment(sketch, "E199", {"start": v(-711.2, -514.35) * mm, "end": v(-711.2, -736.6) * mm});
            skLineSegment(sketch, "E200", {"start": v(711.2, -736.6) * mm, "end": v(711.2, -514.35) * mm});
            skLineSegment(sketch, "E201", {"start": v(711.2, -330.2) * mm, "end": v(711.2, -107.95) * mm});
            skPoint(sketch, "E202.visualSharp", {"position": v(-762, 152.4) * mm});
            skArc(sketch, "E202.filletArc", {"start": v(-660.4, 152.4) * mm, "mid": v(-732.24, 122.64) * mm, "end": v(-762, 50.8) * mm});
            skPoint(sketch, "E203.visualSharp", {"position": v(765.01, 152.4) * mm});
            skArc(sketch, "E203.filletArc", {"start": v(763.82, 49.62) * mm, "mid": v(734.49, 122.22) * mm, "end": v(662.23, 152.4) * mm});
            skLineSegment(sketch, "E204", {"start": v(0, 152.4) * mm, "end": v(0.92, -914.4) * mm, "construction": true});
            skPoint(sketch, "E204.endSnap0", {"position": v(0.92, 152.4) * mm});
            skLineSegment(sketch, "E205", {"start": v(-762, 0) * mm, "end": v(763.25, 0) * mm, "construction": true});
            skSolve(sketch);
        }
        {
            var Q0;
            Q0 = qSketchRegion(id + "F9", true);
            extrude(context, id + "F10", {"entities" : qUnion([Q0]), "operationType" : NewBodyOperationType.ADD, "oppositeDirection" : true, "depth" : 25.4 * mm});
        }
        {
            var Q0;
            {var subQ0=makeQuery(id+"F7.opExtrude","SWEPT_FACE",FACE,{"disambiguationData":[OSD([sQuery(id+"F6.wireOp",EDGE,"E167")])]});var subQ1=makeQuery(id+"F7.opExtrude","SWEPT_FACE",FACE,{"disambiguationData":[OSD([sQuery(id+"F6.wireOp",EDGE,"E166.trimOffspring")])]});Q0=makeQuery(id+"F10.boolean.opBoolean","MERGE",FACE,{"derivedFrom":[subQ1,subQ0,makeQuery(id+"F8.opPattern","COPY",FACE,{"derivedFrom":subQ1,"instanceName":"1"}),makeQuery(id+"F8.opPattern","COPY",FACE,{"derivedFrom":subQ0,"instanceName":"1"}),makeQuery(id+"F10.opExtrude","CAP_FACE",FACE,{"disambiguationData":[OSD([sQuery(id+"F9.wireOp",EDGE,"E168.0"),sQuery(id+"F9.wireOp",EDGE,"E169.0"),sQuery(id+"F9.wireOp",EDGE,"E170.0"),sQuery(id+"F9.wireOp",EDGE,"E171.0"),sQuery(id+"F9.wireOp",EDGE,"E172.0"),sQuery(id+"F9.wireOp",EDGE,"E173.0"),sQuery(id+"F9.wireOp",EDGE,"E174.0"),sQuery(id+"F9.wireOp",EDGE,"E175.0"),sQuery(id+"F9.wireOp",EDGE,"E176.0"),sQuery(id+"F9.wireOp",EDGE,"E177.0"),sQuery(id+"F9.wireOp",EDGE,"E178.0"),sQuery(id+"F9.wireOp",EDGE,"E179.0"),sQuery(id+"F9.wireOp",EDGE,"E180.0"),sQuery(id+"F9.wireOp",EDGE,"E181.0"),sQuery(id+"F9.wireOp",EDGE,"E182.0"),sQuery(id+"F9.wireOp",EDGE,"E183.0"),sQuery(id+"F9.wireOp",EDGE,"E184.0"),sQuery(id+"F9.wireOp",EDGE,"E185.0"),sQuery(id+"F9.wireOp",EDGE,"E186.0"),sQuery(id+"F9.wireOp",EDGE,"E187.0"),sQuery(id+"F9.wireOp",EDGE,"E188.0"),sQuery(id+"F9.wireOp",EDGE,"E189.0"),sQuery(id+"F9.wireOp",EDGE,"E190.0"),sQuery(id+"F9.wireOp",EDGE,"E191.0"),sQuery(id+"F9.wireOp",EDGE,"E192.0"),sQuery(id+"F9.wireOp",EDGE,"E195"),sQuery(id+"F9.wireOp",EDGE,"E196"),sQuery(id+"F9.wireOp",EDGE,"E197"),sQuery(id+"F9.wireOp",EDGE,"E198"),sQuery(id+"F9.wireOp",EDGE,"E199"),sQuery(id+"F9.wireOp",EDGE,"E200"),sQuery(id+"F9.wireOp",EDGE,"E201"),sQuery(id+"F9.wireOp",EDGE,"E202.filletArc"),sQuery(id+"F9.wireOp",EDGE,"E203.filletArc")])],"isStart":true})]});}
            var sketch = newSketch(context, id + "F11", { "sketchPlane" : qUnion([Q0])});
            skLineSegment(sketch, "E206.0", {"start": v(-584.2, 25.4) * mm, "end": v(-584.2, -660.4) * mm});
            skLineSegment(sketch, "E207.0", {"start": v(-533.4, 25.4) * mm, "end": v(-533.4, -660.4) * mm});
            skArc(sketch, "E208.0", {"start": v(-584.2, -660.4) * mm, "mid": v(-558.8, -685.8) * mm, "end": v(-533.4, -660.4) * mm});
            skLineSegment(sketch, "E209", {"start": v(-558.8, 50.8) * mm, "end": v(-558.8, 50.8) * mm});
            skPoint(sketch, "E210.orphan", {"position": v(-584.2, 177.8) * mm});
            skPoint(sketch, "E211.orphan", {"position": v(-533.4, 177.8) * mm});
            skPoint(sketch, "E212.visualSharp", {"position": v(-584.2, 50.8) * mm});
            skArc(sketch, "E212.filletArc", {"start": v(-558.8, 50.8) * mm, "mid": v(-576.76, 43.36) * mm, "end": v(-584.2, 25.4) * mm});
            skPoint(sketch, "E213.visualSharp", {"position": v(-533.4, 50.8) * mm});
            skArc(sketch, "E213.filletArc", {"start": v(-533.4, 25.4) * mm, "mid": v(-540.84, 43.36) * mm, "end": v(-558.8, 50.8) * mm});
            skLineSegment(sketch, "E214.1.0.0", {"start": v(-431.8, 25.4) * mm, "end": v(-431.8, -660.4) * mm});
            skArc(sketch, "E214.1.0.1", {"start": v(-482.6, -660.4) * mm, "mid": v(-457.2, -685.8) * mm, "end": v(-431.8, -660.4) * mm});
            skLineSegment(sketch, "E214.1.0.2", {"start": v(-482.6, 25.4) * mm, "end": v(-482.6, -660.4) * mm});
            skPoint(sketch, "E214.1.0.3", {"position": v(-431.8, 50.8) * mm});
            skPoint(sketch, "E214.1.0.4", {"position": v(-482.6, 50.8) * mm});
            skArc(sketch, "E214.1.0.5", {"start": v(-457.2, 50.8) * mm, "mid": v(-475.16, 43.36) * mm, "end": v(-482.6, 25.4) * mm});
            skArc(sketch, "E214.1.0.6", {"start": v(-431.8, 25.4) * mm, "mid": v(-439.24, 43.36) * mm, "end": v(-457.2, 50.8) * mm});
            skLineSegment(sketch, "E214.2.0.0", {"start": v(-330.2, 25.4) * mm, "end": v(-330.2, -660.4) * mm});
            skArc(sketch, "E214.2.0.1", {"start": v(-381, -660.4) * mm, "mid": v(-355.6, -685.8) * mm, "end": v(-330.2, -660.4) * mm});
            skLineSegment(sketch, "E214.2.0.2", {"start": v(-381, 25.4) * mm, "end": v(-381, -660.4) * mm});
            skPoint(sketch, "E214.2.0.3", {"position": v(-330.2, 50.8) * mm});
            skPoint(sketch, "E214.2.0.4", {"position": v(-381, 50.8) * mm});
            skArc(sketch, "E214.2.0.5", {"start": v(-355.6, 50.8) * mm, "mid": v(-373.56, 43.36) * mm, "end": v(-381, 25.4) * mm});
            skArc(sketch, "E214.2.0.6", {"start": v(-330.2, 25.4) * mm, "mid": v(-337.64, 43.36) * mm, "end": v(-355.6, 50.8) * mm});
            skLineSegment(sketch, "E214.3.0.0", {"start": v(-228.6, 25.4) * mm, "end": v(-228.6, -660.4) * mm});
            skArc(sketch, "E214.3.0.1", {"start": v(-279.4, -660.4) * mm, "mid": v(-254, -685.8) * mm, "end": v(-228.6, -660.4) * mm});
            skLineSegment(sketch, "E214.3.0.2", {"start": v(-279.4, 25.4) * mm, "end": v(-279.4, -660.4) * mm});
            skPoint(sketch, "E214.3.0.3", {"position": v(-228.6, 50.8) * mm});
            skPoint(sketch, "E214.3.0.4", {"position": v(-279.4, 50.8) * mm});
            skArc(sketch, "E214.3.0.5", {"start": v(-254, 50.8) * mm, "mid": v(-271.96, 43.36) * mm, "end": v(-279.4, 25.4) * mm});
            skArc(sketch, "E214.3.0.6", {"start": v(-228.6, 25.4) * mm, "mid": v(-236.04, 43.36) * mm, "end": v(-254, 50.8) * mm});
            skLineSegment(sketch, "E214.4.0.0", {"start": v(-127, 25.4) * mm, "end": v(-127, -660.4) * mm});
            skArc(sketch, "E214.4.0.1", {"start": v(-177.8, -660.4) * mm, "mid": v(-152.4, -685.8) * mm, "end": v(-127, -660.4) * mm});
            skLineSegment(sketch, "E214.4.0.2", {"start": v(-177.8, 25.4) * mm, "end": v(-177.8, -660.4) * mm});
            skPoint(sketch, "E214.4.0.3", {"position": v(-127, 50.8) * mm});
            skPoint(sketch, "E214.4.0.4", {"position": v(-177.8, 50.8) * mm});
            skArc(sketch, "E214.4.0.5", {"start": v(-152.4, 50.8) * mm, "mid": v(-170.36, 43.36) * mm, "end": v(-177.8, 25.4) * mm});
            skArc(sketch, "E214.4.0.6", {"start": v(-127, 25.4) * mm, "mid": v(-134.44, 43.36) * mm, "end": v(-152.4, 50.8) * mm});
            skLineSegment(sketch, "E214.5.0.0", {"start": v(-25.4, 25.4) * mm, "end": v(-25.4, -660.4) * mm});
            skArc(sketch, "E214.5.0.1", {"start": v(-76.2, -660.4) * mm, "mid": v(-50.8, -685.8) * mm, "end": v(-25.4, -660.4) * mm});
            skLineSegment(sketch, "E214.5.0.2", {"start": v(-76.2, 25.4) * mm, "end": v(-76.2, -660.4) * mm});
            skPoint(sketch, "E214.5.0.3", {"position": v(-25.4, 50.8) * mm});
            skPoint(sketch, "E214.5.0.4", {"position": v(-76.2, 50.8) * mm});
            skArc(sketch, "E214.5.0.5", {"start": v(-50.8, 50.8) * mm, "mid": v(-68.76, 43.36) * mm, "end": v(-76.2, 25.4) * mm});
            skArc(sketch, "E214.5.0.6", {"start": v(-25.4, 25.4) * mm, "mid": v(-32.84, 43.36) * mm, "end": v(-50.8, 50.8) * mm});
            skLineSegment(sketch, "E214.6.0.0", {"start": v(76.2, 25.4) * mm, "end": v(76.2, -660.4) * mm});
            skArc(sketch, "E214.6.0.1", {"start": v(25.4, -660.4) * mm, "mid": v(50.8, -685.8) * mm, "end": v(76.2, -660.4) * mm});
            skLineSegment(sketch, "E214.6.0.2", {"start": v(25.4, 25.4) * mm, "end": v(25.4, -660.4) * mm});
            skPoint(sketch, "E214.6.0.3", {"position": v(76.2, 50.8) * mm});
            skPoint(sketch, "E214.6.0.4", {"position": v(25.4, 50.8) * mm});
            skArc(sketch, "E214.6.0.5", {"start": v(50.8, 50.8) * mm, "mid": v(32.84, 43.36) * mm, "end": v(25.4, 25.4) * mm});
            skArc(sketch, "E214.6.0.6", {"start": v(76.2, 25.4) * mm, "mid": v(68.76, 43.36) * mm, "end": v(50.8, 50.8) * mm});
            skLineSegment(sketch, "E214.7.0.0", {"start": v(177.8, 25.4) * mm, "end": v(177.8, -660.4) * mm});
            skArc(sketch, "E214.7.0.1", {"start": v(127, -660.4) * mm, "mid": v(152.4, -685.8) * mm, "end": v(177.8, -660.4) * mm});
            skLineSegment(sketch, "E214.7.0.2", {"start": v(127, 25.4) * mm, "end": v(127, -660.4) * mm});
            skPoint(sketch, "E214.7.0.3", {"position": v(177.8, 50.8) * mm});
            skPoint(sketch, "E214.7.0.4", {"position": v(127, 50.8) * mm});
            skArc(sketch, "E214.7.0.5", {"start": v(152.4, 50.8) * mm, "mid": v(134.44, 43.36) * mm, "end": v(127, 25.4) * mm});
            skArc(sketch, "E214.7.0.6", {"start": v(177.8, 25.4) * mm, "mid": v(170.36, 43.36) * mm, "end": v(152.4, 50.8) * mm});
            skLineSegment(sketch, "E214.8.0.0", {"start": v(279.4, 25.4) * mm, "end": v(279.4, -660.4) * mm});
            skArc(sketch, "E214.8.0.1", {"start": v(228.6, -660.4) * mm, "mid": v(254, -685.8) * mm, "end": v(279.4, -660.4) * mm});
            skLineSegment(sketch, "E214.8.0.2", {"start": v(228.6, 25.4) * mm, "end": v(228.6, -660.4) * mm});
            skPoint(sketch, "E214.8.0.3", {"position": v(279.4, 50.8) * mm});
            skPoint(sketch, "E214.8.0.4", {"position": v(228.6, 50.8) * mm});
            skArc(sketch, "E214.8.0.5", {"start": v(254, 50.8) * mm, "mid": v(236.04, 43.36) * mm, "end": v(228.6, 25.4) * mm});
            skArc(sketch, "E214.8.0.6", {"start": v(279.4, 25.4) * mm, "mid": v(271.96, 43.36) * mm, "end": v(254, 50.8) * mm});
            skLineSegment(sketch, "E214.9.0.0", {"start": v(381, 25.4) * mm, "end": v(381, -660.4) * mm});
            skArc(sketch, "E214.9.0.1", {"start": v(330.2, -660.4) * mm, "mid": v(355.6, -685.8) * mm, "end": v(381, -660.4) * mm});
            skLineSegment(sketch, "E214.9.0.2", {"start": v(330.2, 25.4) * mm, "end": v(330.2, -660.4) * mm});
            skPoint(sketch, "E214.9.0.3", {"position": v(381, 50.8) * mm});
            skPoint(sketch, "E214.9.0.4", {"position": v(330.2, 50.8) * mm});
            skArc(sketch, "E214.9.0.5", {"start": v(355.6, 50.8) * mm, "mid": v(337.64, 43.36) * mm, "end": v(330.2, 25.4) * mm});
            skArc(sketch, "E214.9.0.6", {"start": v(381, 25.4) * mm, "mid": v(373.56, 43.36) * mm, "end": v(355.6, 50.8) * mm});
            skLineSegment(sketch, "E214.10.0.0", {"start": v(482.6, 25.4) * mm, "end": v(482.6, -660.4) * mm});
            skArc(sketch, "E214.10.0.1", {"start": v(431.8, -660.4) * mm, "mid": v(457.2, -685.8) * mm, "end": v(482.6, -660.4) * mm});
            skLineSegment(sketch, "E214.10.0.2", {"start": v(431.8, 25.4) * mm, "end": v(431.8, -660.4) * mm});
            skPoint(sketch, "E214.10.0.3", {"position": v(482.6, 50.8) * mm});
            skPoint(sketch, "E214.10.0.4", {"position": v(431.8, 50.8) * mm});
            skArc(sketch, "E214.10.0.5", {"start": v(457.2, 50.8) * mm, "mid": v(439.24, 43.36) * mm, "end": v(431.8, 25.4) * mm});
            skArc(sketch, "E214.10.0.6", {"start": v(482.6, 25.4) * mm, "mid": v(475.16, 43.36) * mm, "end": v(457.2, 50.8) * mm});
            skLineSegment(sketch, "E214.11.0.0", {"start": v(584.2, 25.4) * mm, "end": v(584.2, -660.4) * mm});
            skArc(sketch, "E214.11.0.1", {"start": v(533.4, -660.4) * mm, "mid": v(558.8, -685.8) * mm, "end": v(584.2, -660.4) * mm});
            skLineSegment(sketch, "E214.11.0.2", {"start": v(533.4, 25.4) * mm, "end": v(533.4, -660.4) * mm});
            skPoint(sketch, "E214.11.0.3", {"position": v(584.2, 50.8) * mm});
            skPoint(sketch, "E214.11.0.4", {"position": v(533.4, 50.8) * mm});
            skArc(sketch, "E214.11.0.5", {"start": v(558.8, 50.8) * mm, "mid": v(540.84, 43.36) * mm, "end": v(533.4, 25.4) * mm});
            skArc(sketch, "E214.11.0.6", {"start": v(584.2, 25.4) * mm, "mid": v(576.76, 43.36) * mm, "end": v(558.8, 50.8) * mm});
            skLineSegment(sketch, "E214.direction1", {"start": v(-584.2, -660.4) * mm, "end": v(-482.6, -660.4) * mm, "construction": true});
            skLineSegment(sketch, "E215", {"start": v(0.92, 152.4) * mm, "end": v(0.92, -914.4) * mm, "construction": true});
            skLineSegment(sketch, "E216", {"start": v(-762, 0) * mm, "end": v(763.25, 0) * mm, "construction": true});
            skSolve(sketch);
        }
        {
            var Q0;
            Q0 = qSketchRegion(id + "F11", true);
            extrude(context, id + "F12", {"entities" : qUnion([Q0]), "operationType" : NewBodyOperationType.REMOVE, "oppositeDirection" : true, "depth" : 152.4 * mm});
        }
        {
            var Q0;
            Q0=makeQuery(id+"F7.opExtrude","CAP_FACE",FACE,{"disambiguationData":[OSD([sQuery(id+"F6.wireOp",EDGE,"E125.bottom"),sQuery(id+"F6.wireOp",EDGE,"E125.top"),sQuery(id+"F6.wireOp",EDGE,"E126"),sQuery(id+"F6.wireOp",EDGE,"E127"),sQuery(id+"F6.wireOp",EDGE,"E128"),sQuery(id+"F6.wireOp",EDGE,"E129"),sQuery(id+"F6.wireOp",EDGE,"E133"),sQuery(id+"F6.wireOp",EDGE,"E134"),sQuery(id+"F6.wireOp",EDGE,"E135"),sQuery(id+"F6.wireOp",EDGE,"E136.filletArc"),sQuery(id+"F6.wireOp",EDGE,"E137.filletArc"),sQuery(id+"F6.wireOp",EDGE,"E138.filletArc"),sQuery(id+"F6.wireOp",EDGE,"E139.filletArc"),sQuery(id+"F6.wireOp",EDGE,"E140.filletArc"),sQuery(id+"F6.wireOp",EDGE,"E141"),sQuery(id+"F6.wireOp",EDGE,"E142.filletArc"),sQuery(id+"F6.wireOp",EDGE,"E143"),sQuery(id+"F6.wireOp",EDGE,"E145.MirrorCS"),sQuery(id+"F6.wireOp",EDGE,"E146.MirrorCS"),sQuery(id+"F6.wireOp",EDGE,"E147.MirrorCS"),sQuery(id+"F6.wireOp",EDGE,"E148.MirrorCS"),sQuery(id+"F6.wireOp",EDGE,"E149.MirrorCS"),sQuery(id+"F6.wireOp",EDGE,"E150.MirrorCS"),sQuery(id+"F6.wireOp",EDGE,"E151.MirrorCS"),sQuery(id+"F6.wireOp",EDGE,"E156.MirrorCS"),sQuery(id+"F6.wireOp",EDGE,"E157.MirrorCS"),sQuery(id+"F6.wireOp",EDGE,"E158.MirrorCS"),sQuery(id+"F6.wireOp",EDGE,"E159.MirrorCS"),sQuery(id+"F6.wireOp",EDGE,"E160.MirrorCS"),sQuery(id+"F6.wireOp",EDGE,"E162.MirrorCS"),sQuery(id+"F6.wireOp",EDGE,"E166.trimOffspring"),sQuery(id+"F6.wireOp",EDGE,"E167")])],"isStart":false});
            var sketch = newSketch(context, id + "F13", { "sketchPlane" : qUnion([Q0])});
            skLineSegment(sketch, "E217.0", {"start": v(19.05, 0) * mm, "end": v(723.9, 0) * mm});
            skPoint(sketch, "E218.0", {"position": v(749.3, 152.4) * mm});
            skPoint(sketch, "E219.0", {"position": v(723.9, 152.4) * mm});
            skLineSegment(sketch, "E220", {"start": v(622.3, 152.4) * mm, "end": v(120.65, 152.4) * mm});
            skLineSegment(sketch, "E221", {"start": v(19.05, 50.8) * mm, "end": v(19.05, 0) * mm});
            skLineSegment(sketch, "E222", {"start": v(723.9, 50.8) * mm, "end": v(723.9, 0) * mm});
            skPoint(sketch, "E223.visualSharp", {"position": v(19.05, 152.4) * mm});
            skArc(sketch, "E223.filletArc", {"start": v(120.65, 152.4) * mm, "mid": v(48.8, 122.64) * mm, "end": v(19.05, 50.8) * mm});
            skArc(sketch, "E224.filletArc", {"start": v(723.9, 50.8) * mm, "mid": v(694.14, 122.64) * mm, "end": v(622.3, 152.4) * mm});
            skSolve(sketch);
        }
        {
            var Q0;
            Q0 = qSketchRegion(id + "F13", true);
            var Q1;
            {var subQ0=sQuery(id+"F6.wireOp",EDGE,"E125.top");var subQ2=sQuery(id+"F0.wireOp",EDGE,"E2.top");var subQ3=makeQuery(id+"F1.opExtrude","SWEPT_FACE",FACE,{"disambiguationData":[OSD([subQ2])]});var subQ4=sQuery(id+"F6.wireOp",EDGE,"E125.bottom");var subQ12=sQuery(id+"F6.wireOp",EDGE,"E149.MirrorCS");var subQ13=sQuery(id+"F6.wireOp",EDGE,"E158.MirrorCS");var subQ14=sQuery(id+"F6.wireOp",EDGE,"E148.MirrorCS");var subQ15=sQuery(id+"F6.wireOp",EDGE,"E147.MirrorCS");var subQ16=sQuery(id+"F6.wireOp",EDGE,"E146.MirrorCS");var subQ17=sQuery(id+"F6.wireOp",EDGE,"E150.MirrorCS");var subQ18=sQuery(id+"F6.wireOp",EDGE,"E166.trimOffspring");var subQ19=sQuery(id+"F6.wireOp",EDGE,"E145.MirrorCS");var subQ20=sQuery(id+"F6.wireOp",EDGE,"E151.MirrorCS");var subQ21=sQuery(id+"F6.wireOp",EDGE,"E167");var subQ22=sQuery(id+"F6.wireOp",EDGE,"E162.MirrorCS");var subQ23=sQuery(id+"F6.wireOp",EDGE,"E156.MirrorCS");var subQ24=sQuery(id+"F6.wireOp",EDGE,"E157.MirrorCS");var subQ25=sQuery(id+"F6.wireOp",EDGE,"E159.MirrorCS");var subQ26=sQuery(id+"F6.wireOp",EDGE,"E160.MirrorCS");Q1=makeQuery(id+"F10.boolean.opBoolean","SPLIT",FACE,{"disambiguationData":[TD([subQ3])],"derivedFrom":makeQuery(id+"F7.boolean.opBoolean","SPLIT",FACE,{"disambiguationData":[TD([subQ3])],"derivedFrom":makeQuery(id+"F7.opExtrude","CAP_FACE",FACE,{"disambiguationData":[OSD([subQ4,subQ0,sQuery(id+"F6.wireOp",EDGE,"E126"),sQuery(id+"F6.wireOp",EDGE,"E127"),sQuery(id+"F6.wireOp",EDGE,"E128"),sQuery(id+"F6.wireOp",EDGE,"E129"),sQuery(id+"F6.wireOp",EDGE,"E133"),sQuery(id+"F6.wireOp",EDGE,"E134"),sQuery(id+"F6.wireOp",EDGE,"E135"),sQuery(id+"F6.wireOp",EDGE,"E136.filletArc"),sQuery(id+"F6.wireOp",EDGE,"E137.filletArc"),sQuery(id+"F6.wireOp",EDGE,"E138.filletArc"),sQuery(id+"F6.wireOp",EDGE,"E139.filletArc"),sQuery(id+"F6.wireOp",EDGE,"E140.filletArc"),sQuery(id+"F6.wireOp",EDGE,"E141"),sQuery(id+"F6.wireOp",EDGE,"E142.filletArc"),sQuery(id+"F6.wireOp",EDGE,"E143"),subQ19,subQ16,subQ15,subQ14,subQ12,subQ17,subQ20,subQ23,subQ24,subQ13,subQ25,subQ26,subQ22,subQ18,subQ21])],"isStart":true})})});}
            extrude(context, id + "F14", {"entities" : qUnion([Q0]), "operationType" : NewBodyOperationType.ADD, "endBound" : BoundingType.UP_TO_SURFACE, "oppositeDirection" : true, "endBoundEntityFace" : qUnion([Q1]), "depth" : 25.4 * mm});
        }
        {
            var Q0;
            Q0=makeQuery(id+"F1.opExtrude","SWEPT_BODY",BODY,{"disambiguationData":[OSD([sQuery(id+"F0.wireOp",EDGE,"E2.bottom"),sQuery(id+"F0.wireOp",EDGE,"E2.top"),sQuery(id+"F0.wireOp",EDGE,"E2.left"),sQuery(id+"F0.wireOp",EDGE,"E2.right"),sQuery(id+"F0.wireOp",EDGE,"E3.filletArc"),sQuery(id+"F0.wireOp",EDGE,"E4.filletArc")])]});
            var Q1;
            Q1=qCreatedBy(makeId("Right.planeOp"),FACE);
            mirror(context, id + "F15", {"operationType" : NewBodyOperationType.ADD, "entities" : qUnion([Q0]), "mirrorPlane" : qUnion([Q1])});
        }
        {
            var Q0;
            Q0=makeQuery(id+"F14.boolean.opBoolean","MERGE",FACE,{"derivedFrom":[makeQuery(id+"F7.opExtrude","CAP_FACE",FACE,{"disambiguationData":[OSD([sQuery(id+"F6.wireOp",EDGE,"E125.bottom"),sQuery(id+"F6.wireOp",EDGE,"E125.top"),sQuery(id+"F6.wireOp",EDGE,"E126"),sQuery(id+"F6.wireOp",EDGE,"E127"),sQuery(id+"F6.wireOp",EDGE,"E128"),sQuery(id+"F6.wireOp",EDGE,"E129"),sQuery(id+"F6.wireOp",EDGE,"E133"),sQuery(id+"F6.wireOp",EDGE,"E134"),sQuery(id+"F6.wireOp",EDGE,"E135"),sQuery(id+"F6.wireOp",EDGE,"E136.filletArc"),sQuery(id+"F6.wireOp",EDGE,"E137.filletArc"),sQuery(id+"F6.wireOp",EDGE,"E138.filletArc"),sQuery(id+"F6.wireOp",EDGE,"E139.filletArc"),sQuery(id+"F6.wireOp",EDGE,"E140.filletArc"),sQuery(id+"F6.wireOp",EDGE,"E141"),sQuery(id+"F6.wireOp",EDGE,"E142.filletArc"),sQuery(id+"F6.wireOp",EDGE,"E143"),sQuery(id+"F6.wireOp",EDGE,"E145.MirrorCS"),sQuery(id+"F6.wireOp",EDGE,"E146.MirrorCS"),sQuery(id+"F6.wireOp",EDGE,"E147.MirrorCS"),sQuery(id+"F6.wireOp",EDGE,"E148.MirrorCS"),sQuery(id+"F6.wireOp",EDGE,"E149.MirrorCS"),sQuery(id+"F6.wireOp",EDGE,"E150.MirrorCS"),sQuery(id+"F6.wireOp",EDGE,"E151.MirrorCS"),sQuery(id+"F6.wireOp",EDGE,"E156.MirrorCS"),sQuery(id+"F6.wireOp",EDGE,"E157.MirrorCS"),sQuery(id+"F6.wireOp",EDGE,"E158.MirrorCS"),sQuery(id+"F6.wireOp",EDGE,"E159.MirrorCS"),sQuery(id+"F6.wireOp",EDGE,"E160.MirrorCS"),sQuery(id+"F6.wireOp",EDGE,"E162.MirrorCS"),sQuery(id+"F6.wireOp",EDGE,"E166.trimOffspring"),sQuery(id+"F6.wireOp",EDGE,"E167")])],"isStart":false}),makeQuery(id+"F14.opExtrude","CAP_FACE",FACE,{"disambiguationData":[OSD([sQuery(id+"F13.wireOp",EDGE,"E217.0"),sQuery(id+"F13.wireOp",EDGE,"E220"),sQuery(id+"F13.wireOp",EDGE,"E221"),sQuery(id+"F13.wireOp",EDGE,"E222"),sQuery(id+"F13.wireOp",EDGE,"E223.filletArc"),sQuery(id+"F13.wireOp",EDGE,"E224.filletArc")])],"isStart":true})]});
            var sketch = newSketch(context, id + "F16", { "sketchPlane" : qUnion([Q0])});
            skLineSegment(sketch, "E225", {"start": v(371.48, 152.4) * mm, "end": v(371.48, -914.4) * mm, "construction": true});
            skLineSegment(sketch, "E226.bottom", {"start": v(320.68, 50.8) * mm, "end": v(320.68, 50.8) * mm});
            skLineSegment(sketch, "E226.top", {"start": v(320.68, -685.8) * mm, "end": v(320.68, -685.8) * mm});
            skLineSegment(sketch, "E226.left", {"start": v(346.08, 25.4) * mm, "end": v(346.08, -660.4) * mm});
            skLineSegment(sketch, "E226.right", {"start": v(295.28, 25.4) * mm, "end": v(295.28, -660.4) * mm});
            skPoint(sketch, "E227.visualSharp", {"position": v(295.28, 50.8) * mm});
            skArc(sketch, "E227.filletArc", {"start": v(320.68, 50.8) * mm, "mid": v(302.71, 43.36) * mm, "end": v(295.28, 25.4) * mm});
            skPoint(sketch, "E228.visualSharp", {"position": v(346.08, 50.8) * mm});
            skArc(sketch, "E228.filletArc", {"start": v(346.08, 25.4) * mm, "mid": v(338.64, 43.36) * mm, "end": v(320.68, 50.8) * mm});
            skPoint(sketch, "E229.visualSharp", {"position": v(295.28, -685.8) * mm});
            skArc(sketch, "E229.filletArc", {"start": v(295.28, -660.4) * mm, "mid": v(302.71, -678.36) * mm, "end": v(320.68, -685.8) * mm});
            skPoint(sketch, "E230.visualSharp", {"position": v(346.08, -685.8) * mm});
            skArc(sketch, "E230.filletArc", {"start": v(320.68, -685.8) * mm, "mid": v(338.64, -678.36) * mm, "end": v(346.08, -660.4) * mm});
            skLineSegment(sketch, "E231.1.0.0", {"start": v(193.68, 25.4) * mm, "end": v(193.68, -660.4) * mm});
            skLineSegment(sketch, "E231.1.0.1", {"start": v(244.48, 25.4) * mm, "end": v(244.48, -660.4) * mm});
            skPoint(sketch, "E231.1.0.2", {"position": v(244.47, 50.8) * mm});
            skPoint(sketch, "E231.1.0.3", {"position": v(244.48, -685.8) * mm});
            skPoint(sketch, "E231.1.0.4", {"position": v(193.68, -685.8) * mm});
            skPoint(sketch, "E231.1.0.5", {"position": v(193.67, 50.8) * mm});
            skArc(sketch, "E231.1.0.6", {"start": v(193.68, -660.4) * mm, "mid": v(201.11, -678.36) * mm, "end": v(219.08, -685.8) * mm});
            skArc(sketch, "E231.1.0.7", {"start": v(219.07, 50.8) * mm, "mid": v(201.11, 43.36) * mm, "end": v(193.67, 25.4) * mm});
            skArc(sketch, "E231.1.0.8", {"start": v(219.08, -685.8) * mm, "mid": v(237.04, -678.36) * mm, "end": v(244.48, -660.4) * mm});
            skArc(sketch, "E231.1.0.9", {"start": v(244.48, 25.4) * mm, "mid": v(237.04, 43.36) * mm, "end": v(219.08, 50.8) * mm});
            skLineSegment(sketch, "E231.2.0.0", {"start": v(92.08, 25.4) * mm, "end": v(92.08, -660.4) * mm});
            skLineSegment(sketch, "E231.2.0.1", {"start": v(142.88, 25.4) * mm, "end": v(142.88, -660.4) * mm});
            skPoint(sketch, "E231.2.0.2", {"position": v(142.87, 50.8) * mm});
            skPoint(sketch, "E231.2.0.3", {"position": v(142.88, -685.8) * mm});
            skPoint(sketch, "E231.2.0.4", {"position": v(92.08, -685.8) * mm});
            skPoint(sketch, "E231.2.0.5", {"position": v(92.07, 50.8) * mm});
            skArc(sketch, "E231.2.0.6", {"start": v(92.08, -660.4) * mm, "mid": v(99.51, -678.36) * mm, "end": v(117.48, -685.8) * mm});
            skArc(sketch, "E231.2.0.7", {"start": v(117.47, 50.8) * mm, "mid": v(99.51, 43.36) * mm, "end": v(92.07, 25.4) * mm});
            skArc(sketch, "E231.2.0.8", {"start": v(117.48, -685.8) * mm, "mid": v(135.44, -678.36) * mm, "end": v(142.88, -660.4) * mm});
            skArc(sketch, "E231.2.0.9", {"start": v(142.88, 25.4) * mm, "mid": v(135.44, 43.36) * mm, "end": v(117.47, 50.8) * mm});
            skLineSegment(sketch, "E231.direction1", {"start": v(295.28, -685.8) * mm, "end": v(193.68, -685.8) * mm, "construction": true});
            skArc(sketch, "E232.MirrorCS", {"start": v(600.08, 25.4) * mm, "mid": v(607.51, 43.36) * mm, "end": v(625.48, 50.8) * mm});
            skArc(sketch, "E233.MirrorCS", {"start": v(625.48, -685.8) * mm, "mid": v(607.51, -678.36) * mm, "end": v(600.08, -660.4) * mm});
            skArc(sketch, "E234.MirrorCS", {"start": v(396.88, 25.4) * mm, "mid": v(404.31, 43.36) * mm, "end": v(422.27, 50.8) * mm});
            skArc(sketch, "E235.MirrorCS", {"start": v(523.88, 50.8) * mm, "mid": v(541.84, 43.36) * mm, "end": v(549.28, 25.4) * mm});
            skArc(sketch, "E236.MirrorCS", {"start": v(549.28, -660.4) * mm, "mid": v(541.84, -678.36) * mm, "end": v(523.88, -685.8) * mm});
            skArc(sketch, "E237.MirrorCS", {"start": v(422.28, -685.8) * mm, "mid": v(404.31, -678.36) * mm, "end": v(396.88, -660.4) * mm});
            skArc(sketch, "E238.MirrorCS", {"start": v(447.68, -660.4) * mm, "mid": v(440.24, -678.36) * mm, "end": v(422.28, -685.8) * mm});
            skArc(sketch, "E239.MirrorCS", {"start": v(498.48, 25.4) * mm, "mid": v(505.91, 43.36) * mm, "end": v(523.88, 50.8) * mm});
            skArc(sketch, "E240.MirrorCS", {"start": v(650.88, -660.4) * mm, "mid": v(643.44, -678.36) * mm, "end": v(625.48, -685.8) * mm});
            skArc(sketch, "E241.MirrorCS", {"start": v(523.88, -685.8) * mm, "mid": v(505.91, -678.36) * mm, "end": v(498.48, -660.4) * mm});
            skArc(sketch, "E242.MirrorCS", {"start": v(422.28, 50.8) * mm, "mid": v(440.24, 43.36) * mm, "end": v(447.68, 25.4) * mm});
            skArc(sketch, "E243.MirrorCS", {"start": v(625.48, 50.8) * mm, "mid": v(643.44, 43.36) * mm, "end": v(650.88, 25.4) * mm});
            skPoint(sketch, "E244.MirrorP", {"position": v(549.27, 50.8) * mm});
            skPoint(sketch, "E245.MirrorP", {"position": v(600.08, -685.8) * mm});
            skPoint(sketch, "E246.MirrorP", {"position": v(549.28, -685.8) * mm});
            skLineSegment(sketch, "E247.MirrorCS", {"start": v(650.88, 25.4) * mm, "end": v(650.87, -660.4) * mm});
            skLineSegment(sketch, "E248.MirrorCS", {"start": v(600.08, 25.4) * mm, "end": v(600.07, -660.4) * mm});
            skPoint(sketch, "E249.MirrorP", {"position": v(498.48, -685.8) * mm});
            skPoint(sketch, "E250.MirrorP", {"position": v(447.68, 50.8) * mm});
            skPoint(sketch, "E251.MirrorP", {"position": v(600.08, 50.8) * mm});
            skPoint(sketch, "E252.MirrorP", {"position": v(447.68, -685.8) * mm});
            skPoint(sketch, "E253.MirrorP", {"position": v(396.88, -685.8) * mm});
            skLineSegment(sketch, "E254.MirrorCS", {"start": v(422.27, 50.8) * mm, "end": v(422.28, 50.8) * mm});
            skLineSegment(sketch, "E255.MirrorCS", {"start": v(498.47, 25.4) * mm, "end": v(498.47, -660.4) * mm});
            skLineSegment(sketch, "E256.MirrorCS", {"start": v(549.27, 25.4) * mm, "end": v(549.27, -660.4) * mm});
            skPoint(sketch, "E257.MirrorP", {"position": v(650.88, 50.8) * mm});
            skPoint(sketch, "E258.MirrorP", {"position": v(650.88, -685.8) * mm});
            skLineSegment(sketch, "E259.MirrorCS", {"start": v(447.68, -685.8) * mm, "end": v(549.28, -685.8) * mm, "construction": true});
            skPoint(sketch, "E260.MirrorP", {"position": v(498.48, 50.8) * mm});
            skLineSegment(sketch, "E261.MirrorCS", {"start": v(396.87, 25.4) * mm, "end": v(396.87, -660.4) * mm});
            skLineSegment(sketch, "E262.MirrorCS", {"start": v(422.28, -685.8) * mm, "end": v(422.28, -685.8) * mm});
            skLineSegment(sketch, "E263.MirrorCS", {"start": v(447.67, 25.4) * mm, "end": v(447.67, -660.4) * mm});
            skPoint(sketch, "E264.MirrorP", {"position": v(396.88, 50.8) * mm});
            skSolve(sketch);
        }
        {
            var Q0;
            Q0 = qSketchRegion(id + "F16", true);
            extrude(context, id + "F17", {"entities" : qUnion([Q0]), "operationType" : NewBodyOperationType.REMOVE, "endBound" : BoundingType.THROUGH_ALL, "oppositeDirection" : true, "depth" : 25.4 * mm});
        }
        {
            var Q0;
            {var subQ0=makeQuery(id+"F7.opExtrude","SWEPT_FACE",FACE,{"disambiguationData":[OSD([sQuery(id+"F6.wireOp",EDGE,"E167")])]});var subQ1=makeQuery(id+"F7.opExtrude","SWEPT_FACE",FACE,{"disambiguationData":[OSD([sQuery(id+"F6.wireOp",EDGE,"E166.trimOffspring")])]});var subQ2=makeQuery(id+"F10.boolean.opBoolean","MERGE",FACE,{"derivedFrom":[subQ1,subQ0,makeQuery(id+"F8.opPattern","COPY",FACE,{"derivedFrom":subQ1,"instanceName":"1"}),makeQuery(id+"F8.opPattern","COPY",FACE,{"derivedFrom":subQ0,"instanceName":"1"}),makeQuery(id+"F10.opExtrude","CAP_FACE",FACE,{"disambiguationData":[OSD([sQuery(id+"F9.wireOp",EDGE,"E168.0"),sQuery(id+"F9.wireOp",EDGE,"E169.0"),sQuery(id+"F9.wireOp",EDGE,"E170.0"),sQuery(id+"F9.wireOp",EDGE,"E171.0"),sQuery(id+"F9.wireOp",EDGE,"E172.0"),sQuery(id+"F9.wireOp",EDGE,"E173.0"),sQuery(id+"F9.wireOp",EDGE,"E174.0"),sQuery(id+"F9.wireOp",EDGE,"E175.0"),sQuery(id+"F9.wireOp",EDGE,"E176.0"),sQuery(id+"F9.wireOp",EDGE,"E177.0"),sQuery(id+"F9.wireOp",EDGE,"E178.0"),sQuery(id+"F9.wireOp",EDGE,"E179.0"),sQuery(id+"F9.wireOp",EDGE,"E180.0"),sQuery(id+"F9.wireOp",EDGE,"E181.0"),sQuery(id+"F9.wireOp",EDGE,"E182.0"),sQuery(id+"F9.wireOp",EDGE,"E183.0"),sQuery(id+"F9.wireOp",EDGE,"E184.0"),sQuery(id+"F9.wireOp",EDGE,"E185.0"),sQuery(id+"F9.wireOp",EDGE,"E186.0"),sQuery(id+"F9.wireOp",EDGE,"E187.0"),sQuery(id+"F9.wireOp",EDGE,"E188.0"),sQuery(id+"F9.wireOp",EDGE,"E189.0"),sQuery(id+"F9.wireOp",EDGE,"E190.0"),sQuery(id+"F9.wireOp",EDGE,"E191.0"),sQuery(id+"F9.wireOp",EDGE,"E192.0"),sQuery(id+"F9.wireOp",EDGE,"E195"),sQuery(id+"F9.wireOp",EDGE,"E196"),sQuery(id+"F9.wireOp",EDGE,"E197"),sQuery(id+"F9.wireOp",EDGE,"E198"),sQuery(id+"F9.wireOp",EDGE,"E199"),sQuery(id+"F9.wireOp",EDGE,"E200"),sQuery(id+"F9.wireOp",EDGE,"E201"),sQuery(id+"F9.wireOp",EDGE,"E202.filletArc"),sQuery(id+"F9.wireOp",EDGE,"E203.filletArc")])],"isStart":true})]});Q0=makeQuery(id+"F15.boolean.opBoolean","MERGE",FACE,{"derivedFrom":[subQ2,makeQuery(id+"F15.opPattern","COPY",FACE,{"derivedFrom":subQ2,"instanceName":"1"})]});}
            var sketch = newSketch(context, id + "F18", { "sketchPlane" : qUnion([Q0])});
            skLineSegment(sketch, "E265.bottom", {"start": v(-711.2, -736.6) * mm, "end": v(711.2, -736.6) * mm});
            skLineSegment(sketch, "E265.top", {"start": v(-711.2, -717.55) * mm, "end": v(711.2, -717.55) * mm});
            skLineSegment(sketch, "E265.left", {"start": v(-711.2, -736.6) * mm, "end": v(-711.2, -717.55) * mm});
            skLineSegment(sketch, "E265.right", {"start": v(711.2, -736.6) * mm, "end": v(711.2, -717.55) * mm});
            skSolve(sketch);
        }
        {
            var Q0;
            Q0 = qSketchRegion(id + "F18", true);
            var Q1;
            {var subQ0=makeQuery(id+"F7.boolean.opBoolean","MERGE",FACE,{"derivedFrom":[makeQuery(id+"F1.opExtrude","CAP_FACE",FACE,{"disambiguationData":[OSD([sQuery(id+"F0.wireOp",EDGE,"E2.bottom"),sQuery(id+"F0.wireOp",EDGE,"E2.top"),sQuery(id+"F0.wireOp",EDGE,"E2.left"),sQuery(id+"F0.wireOp",EDGE,"E2.right"),sQuery(id+"F0.wireOp",EDGE,"E3.filletArc"),sQuery(id+"F0.wireOp",EDGE,"E4.filletArc")])],"isStart":true}),makeQuery(id+"F7.opExtrude","SWEPT_FACE",FACE,{"disambiguationData":[OSD([sQuery(id+"F6.wireOp",EDGE,"E141")])]}),makeQuery(id+"F7.opExtrude","SWEPT_FACE",FACE,{"disambiguationData":[OSD([sQuery(id+"F6.wireOp",EDGE,"E143")])]})]});Q1=makeQuery(id+"F8.boolean.opBoolean","MERGE",FACE,{"derivedFrom":[subQ0,makeQuery(id+"F8.opPattern","COPY",FACE,{"derivedFrom":subQ0,"instanceName":"1"})]});}
            extrude(context, id + "F19", {"entities" : qUnion([Q0]), "operationType" : NewBodyOperationType.ADD, "endBound" : BoundingType.UP_TO_SURFACE, "oppositeDirection" : true, "endBoundEntityFace" : qUnion([Q1]), "depth" : 25.4 * mm});
        }
        {
            var Q0;
            {var subQ30=sQuery(id+"F6.wireOp",EDGE,"E125.top");var subQ35=sQuery(id+"F9.wireOp",EDGE,"E190.0");var subQ37=sQuery(id+"F9.wireOp",EDGE,"E203.filletArc");var subQ45=sQuery(id+"F9.wireOp",EDGE,"E170.0");var subQ48=sQuery(id+"F9.wireOp",EDGE,"E169.0");var subQ50=sQuery(id+"F9.wireOp",EDGE,"E191.0");var subQ52=sQuery(id+"F9.wireOp",EDGE,"E192.0");var subQ54=sQuery(id+"F9.wireOp",EDGE,"E168.0");var subQ55=makeQuery(id+"F10.opExtrude","SWEPT_FACE",FACE,{"disambiguationData":[OSD([subQ54])]});var subQ59=makeQuery(id+"F7.opExtrude","SWEPT_FACE",FACE,{"disambiguationData":[OSD([subQ30])]});var subQ62=sQuery(id+"F9.wireOp",EDGE,"E182.0");var subQ63=sQuery(id+"F9.wireOp",EDGE,"E181.0");var subQ64=sQuery(id+"F9.wireOp",EDGE,"E180.0");var subQ65=sQuery(id+"F9.wireOp",EDGE,"E179.0");var subQ66=sQuery(id+"F9.wireOp",EDGE,"E178.0");var subQ71=sQuery(id+"F9.wireOp",EDGE,"E202.filletArc");var subQ72=sQuery(id+"F9.wireOp",EDGE,"E197");var subQ73=sQuery(id+"F9.wireOp",EDGE,"E196");var subQ74=sQuery(id+"F9.wireOp",EDGE,"E195");var subQ75=makeQuery(id+"F10.opExtrude","CAP_FACE",FACE,{"disambiguationData":[OSD([subQ54,subQ48,subQ45,sQuery(id+"F9.wireOp",EDGE,"E171.0"),sQuery(id+"F9.wireOp",EDGE,"E172.0"),sQuery(id+"F9.wireOp",EDGE,"E173.0"),sQuery(id+"F9.wireOp",EDGE,"E174.0"),sQuery(id+"F9.wireOp",EDGE,"E175.0"),sQuery(id+"F9.wireOp",EDGE,"E176.0"),sQuery(id+"F9.wireOp",EDGE,"E177.0"),subQ66,subQ65,subQ64,subQ63,subQ62,sQuery(id+"F9.wireOp",EDGE,"E183.0"),sQuery(id+"F9.wireOp",EDGE,"E184.0"),sQuery(id+"F9.wireOp",EDGE,"E185.0"),sQuery(id+"F9.wireOp",EDGE,"E186.0"),sQuery(id+"F9.wireOp",EDGE,"E187.0"),sQuery(id+"F9.wireOp",EDGE,"E188.0"),sQuery(id+"F9.wireOp",EDGE,"E189.0"),subQ35,subQ50,subQ52,subQ74,subQ73,subQ72,sQuery(id+"F9.wireOp",EDGE,"E198"),sQuery(id+"F9.wireOp",EDGE,"E199"),sQuery(id+"F9.wireOp",EDGE,"E200"),sQuery(id+"F9.wireOp",EDGE,"E201"),subQ71,subQ37])],"isStart":false});var subQ80=makeQuery(id+"F10.boolean.opBoolean","SPLIT",FACE,{"disambiguationData":[TD([subQ59])],"derivedFrom":subQ75});Q0=makeQuery(id+"F19.boolean.opBoolean","SPLIT",FACE,{"disambiguationData":[TD([subQ55])],"derivedFrom":makeQuery(id+"F15.boolean.opBoolean","MERGE",FACE,{"derivedFrom":[subQ80,makeQuery(id+"F15.opPattern","COPY",FACE,{"derivedFrom":subQ80,"instanceName":"1"})]})});}
            var sketch = newSketch(context, id + "F20", { "sketchPlane" : qUnion([Q0])});
            skLineSegment(sketch, "E266.bottom", {"start": v(692.15, -323.85) * mm, "end": v(-692.15, -323.85) * mm});
            skLineSegment(sketch, "E266.top", {"start": v(692.15, -304.8) * mm, "end": v(-692.15, -304.8) * mm});
            skLineSegment(sketch, "E266.left", {"start": v(692.15, -323.85) * mm, "end": v(692.15, -304.8) * mm});
            skLineSegment(sketch, "E266.right", {"start": v(-692.15, -323.85) * mm, "end": v(-692.15, -304.8) * mm});
            skSolve(sketch);
        }
        {
            var Q0;
            Q0 = qSketchRegion(id + "F20", true);
            var Q1;
            {var subQ64=sQuery(id+"F0.wireOp",EDGE,"E4.filletArc");var subQ67=sQuery(id+"F0.wireOp",EDGE,"E2.bottom");var subQ68=makeQuery(id+"F1.opExtrude","SWEPT_FACE",FACE,{"disambiguationData":[OSD([subQ67])]});var subQ69=sQuery(id+"F0.wireOp",EDGE,"E3.filletArc");var subQ74=sQuery(id+"F0.wireOp",EDGE,"E2.right");var subQ77=sQuery(id+"F0.wireOp",EDGE,"E2.left");var subQ106=sQuery(id+"F0.wireOp",EDGE,"E2.top");var subQ114=makeQuery(id+"F1.opExtrude","CAP_FACE",FACE,{"disambiguationData":[OSD([subQ67,subQ106,subQ77,subQ74,subQ69,subQ64])],"isStart":false});Q1=makeQuery(id+"F19.boolean.opBoolean","SPLIT",FACE,{"disambiguationData":[TD([subQ68])],"derivedFrom":makeQuery(id+"F8.boolean.opBoolean","SPLIT",FACE,{"disambiguationData":[TD([subQ68])],"derivedFrom":makeQuery(id+"F7.boolean.opBoolean","SPLIT",FACE,{"disambiguationData":[TD([subQ68])],"derivedFrom":subQ114})})});}
            extrude(context, id + "F21", {"entities" : qUnion([Q0]), "operationType" : NewBodyOperationType.ADD, "endBound" : BoundingType.UP_TO_SURFACE, "endBoundEntityFace" : qUnion([Q1]), "depth" : 25.4 * mm});
        }
        {
            var Q0;
            Q0=makeQuery(id+"F21.opExtrude","SWEPT_FACE",FACE,{"disambiguationData":[OSD([sQuery(id+"F20.wireOp",EDGE,"E266.top")])]});
            var sketch = newSketch(context, id + "F22", { "sketchPlane" : qUnion([Q0])});
            skLineSegment(sketch, "E267", {"start": v(0, 0) * mm, "end": v(0, -723.9) * mm, "construction": true});
            skLineSegment(sketch, "E268", {"start": v(-692.15, -346.07) * mm, "end": v(692.15, -346.07) * mm, "construction": true});
            skLineSegment(sketch, "E269.bottom", {"start": v(127, -371.47) * mm, "end": v(-127, -371.47) * mm});
            skLineSegment(sketch, "E269.top", {"start": v(127, -320.67) * mm, "end": v(-127, -320.67) * mm});
            skLineSegment(sketch, "E269.left", {"start": v(152.4, -346.07) * mm, "end": v(152.4, -346.07) * mm});
            skLineSegment(sketch, "E269.right", {"start": v(-152.4, -346.07) * mm, "end": v(-152.4, -346.07) * mm});
            skPoint(sketch, "E269.middle", {"position": v(0, -346.07) * mm});
            skPoint(sketch, "E270.visualSharp", {"position": v(-152.4, -320.67) * mm});
            skArc(sketch, "E270.filletArc", {"start": v(-127, -320.67) * mm, "mid": v(-144.96, -328.11) * mm, "end": v(-152.4, -346.07) * mm});
            skPoint(sketch, "E271.visualSharp", {"position": v(152.4, -320.67) * mm});
            skArc(sketch, "E271.filletArc", {"start": v(152.4, -346.07) * mm, "mid": v(144.96, -328.11) * mm, "end": v(127, -320.67) * mm});
            skPoint(sketch, "E272.visualSharp", {"position": v(152.4, -371.47) * mm});
            skArc(sketch, "E272.filletArc", {"start": v(127, -371.47) * mm, "mid": v(144.96, -364.04) * mm, "end": v(152.4, -346.07) * mm});
            skPoint(sketch, "E273.visualSharp", {"position": v(-152.4, -371.47) * mm});
            skArc(sketch, "E273.filletArc", {"start": v(-152.4, -346.07) * mm, "mid": v(-144.96, -364.04) * mm, "end": v(-127, -371.47) * mm});
            skSolve(sketch);
        }
        {
            var Q0;
            Q0 = qSketchRegion(id + "F22", true);
            extrude(context, id + "F23", {"entities" : qUnion([Q0]), "operationType" : NewBodyOperationType.REMOVE, "oppositeDirection" : true, "depth" : 25.4 * mm});
        }
        {
            var Q0;
            Q0=makeQuery(id+"F21.opExtrude","SWEPT_FACE",FACE,{"disambiguationData":[OSD([sQuery(id+"F20.wireOp",EDGE,"E266.top")])]});
            var sketch = newSketch(context, id + "F24", { "sketchPlane" : qUnion([Q0])});
            skLineSegment(sketch, "E274", {"start": v(-692.15, -19.05) * mm, "end": v(692.15, -723.9) * mm, "construction": true});
            skLineSegment(sketch, "E275", {"start": v(692.15, -19.05) * mm, "end": v(-692.15, -723.9) * mm, "construction": true});
            skLineSegment(sketch, "E276", {"start": v(0, -371.47) * mm, "end": v(0, -723.9) * mm, "construction": true});
            skLineSegment(sketch, "E277", {"start": v(0, -371.47) * mm, "end": v(-692.15, -371.48) * mm, "construction": true});
            skLineSegment(sketch, "E278.bottom", {"start": v(628.88, -717.55) * mm, "end": v(-628.88, -717.55) * mm});
            skLineSegment(sketch, "E278.top", {"start": v(628.88, -25.4) * mm, "end": v(-628.88, -25.4) * mm});
            skLineSegment(sketch, "E278.left", {"start": v(679.68, -666.75) * mm, "end": v(679.68, -76.2) * mm});
            skLineSegment(sketch, "E278.right", {"start": v(-679.68, -666.75) * mm, "end": v(-679.68, -76.2) * mm});
            skPoint(sketch, "E278.middle", {"position": v(0, -371.47) * mm});
            skPoint(sketch, "E279.visualSharp", {"position": v(-679.68, -25.4) * mm});
            skArc(sketch, "E279.filletArc", {"start": v(-628.88, -25.4) * mm, "mid": v(-664.8, -40.28) * mm, "end": v(-679.68, -76.2) * mm});
            skPoint(sketch, "E280.visualSharp", {"position": v(679.68, -25.4) * mm});
            skArc(sketch, "E280.filletArc", {"start": v(679.68, -76.2) * mm, "mid": v(664.8, -40.28) * mm, "end": v(628.88, -25.4) * mm});
            skPoint(sketch, "E281.visualSharp", {"position": v(679.68, -717.55) * mm});
            skArc(sketch, "E281.filletArc", {"start": v(628.88, -717.55) * mm, "mid": v(664.8, -702.67) * mm, "end": v(679.68, -666.75) * mm});
            skPoint(sketch, "E282.visualSharp", {"position": v(-679.68, -717.55) * mm});
            skArc(sketch, "E282.filletArc", {"start": v(-679.68, -666.75) * mm, "mid": v(-664.8, -702.67) * mm, "end": v(-628.88, -717.55) * mm});
            skSolve(sketch);
        }
        {
            var Q0;
            Q0 = qSketchRegion(id + "F24", true);
            extrude(context, id + "F25", {"entities" : qUnion([Q0]), "depth" : 152.4 * mm});
        }
        {
            var Q0;
            Q0=makeQuery(id+"F25.opExtrude","CAP_EDGE",EDGE,{"disambiguationData":[OSD([sQuery(id+"F24.wireOp",EDGE,"E278.top")])],"isStart":false});
            fillet(context, id + "F26", {"entities" : qUnion([Q0]), "radius" : 25.4 * mm, "tangentPropagation" : true, "allowEdgeOverflow" : false});
        }
        {
            var Q0;
            {var subQ0=makeQuery(id+"F7.opExtrude","SWEPT_FACE",FACE,{"disambiguationData":[OSD([sQuery(id+"F6.wireOp",EDGE,"E167")])]});var subQ1=makeQuery(id+"F7.opExtrude","SWEPT_FACE",FACE,{"disambiguationData":[OSD([sQuery(id+"F6.wireOp",EDGE,"E166.trimOffspring")])]});var subQ2=makeQuery(id+"F10.boolean.opBoolean","MERGE",FACE,{"derivedFrom":[subQ1,subQ0,makeQuery(id+"F8.opPattern","COPY",FACE,{"derivedFrom":subQ1,"instanceName":"1"}),makeQuery(id+"F8.opPattern","COPY",FACE,{"derivedFrom":subQ0,"instanceName":"1"}),makeQuery(id+"F10.opExtrude","CAP_FACE",FACE,{"disambiguationData":[OSD([sQuery(id+"F9.wireOp",EDGE,"E168.0"),sQuery(id+"F9.wireOp",EDGE,"E169.0"),sQuery(id+"F9.wireOp",EDGE,"E170.0"),sQuery(id+"F9.wireOp",EDGE,"E171.0"),sQuery(id+"F9.wireOp",EDGE,"E172.0"),sQuery(id+"F9.wireOp",EDGE,"E173.0"),sQuery(id+"F9.wireOp",EDGE,"E174.0"),sQuery(id+"F9.wireOp",EDGE,"E175.0"),sQuery(id+"F9.wireOp",EDGE,"E176.0"),sQuery(id+"F9.wireOp",EDGE,"E177.0"),sQuery(id+"F9.wireOp",EDGE,"E178.0"),sQuery(id+"F9.wireOp",EDGE,"E179.0"),sQuery(id+"F9.wireOp",EDGE,"E180.0"),sQuery(id+"F9.wireOp",EDGE,"E181.0"),sQuery(id+"F9.wireOp",EDGE,"E182.0"),sQuery(id+"F9.wireOp",EDGE,"E183.0"),sQuery(id+"F9.wireOp",EDGE,"E184.0"),sQuery(id+"F9.wireOp",EDGE,"E185.0"),sQuery(id+"F9.wireOp",EDGE,"E186.0"),sQuery(id+"F9.wireOp",EDGE,"E187.0"),sQuery(id+"F9.wireOp",EDGE,"E188.0"),sQuery(id+"F9.wireOp",EDGE,"E189.0"),sQuery(id+"F9.wireOp",EDGE,"E190.0"),sQuery(id+"F9.wireOp",EDGE,"E191.0"),sQuery(id+"F9.wireOp",EDGE,"E192.0"),sQuery(id+"F9.wireOp",EDGE,"E195"),sQuery(id+"F9.wireOp",EDGE,"E196"),sQuery(id+"F9.wireOp",EDGE,"E197"),sQuery(id+"F9.wireOp",EDGE,"E198"),sQuery(id+"F9.wireOp",EDGE,"E199"),sQuery(id+"F9.wireOp",EDGE,"E200"),sQuery(id+"F9.wireOp",EDGE,"E201"),sQuery(id+"F9.wireOp",EDGE,"E202.filletArc"),sQuery(id+"F9.wireOp",EDGE,"E203.filletArc")])],"isStart":true})]});Q0=makeQuery(id+"F15.boolean.opBoolean","MERGE",FACE,{"derivedFrom":[subQ2,makeQuery(id+"F15.opPattern","COPY",FACE,{"derivedFrom":subQ2,"instanceName":"1"})]});}
            var sketch = newSketch(context, id + "F27", { "sketchPlane" : qUnion([Q0])});
            skLineSegment(sketch, "E283", {"start": v(0, 0) * mm, "end": v(0, -914.4) * mm, "construction": true});
            skLineSegment(sketch, "E284.bottom", {"start": v(-50.8, -889) * mm, "end": v(-615.95, -889) * mm});
            skLineSegment(sketch, "E284.top", {"start": v(-50.8, -736.6) * mm, "end": v(-269.88, -736.6) * mm});
            skLineSegment(sketch, "E284.left", {"start": v(-25.4, -863.6) * mm, "end": v(-25.4, -762) * mm});
            skLineSegment(sketch, "E285", {"start": v(-641.35, -762) * mm, "end": v(-641.35, -863.6) * mm});
            skPoint(sketch, "E286.visualSharp", {"position": v(-641.35, -736.6) * mm});
            skArc(sketch, "E286.filletArc", {"start": v(-615.95, -736.6) * mm, "mid": v(-633.91, -744.04) * mm, "end": v(-641.35, -762) * mm});
            skPoint(sketch, "E287.visualSharp", {"position": v(-25.4, -736.6) * mm});
            skArc(sketch, "E287.filletArc", {"start": v(-25.4, -762) * mm, "mid": v(-32.84, -744.04) * mm, "end": v(-50.8, -736.6) * mm});
            skPoint(sketch, "E288.visualSharp", {"position": v(-25.4, -889) * mm});
            skArc(sketch, "E288.filletArc", {"start": v(-50.8, -889) * mm, "mid": v(-32.84, -881.56) * mm, "end": v(-25.4, -863.6) * mm});
            skPoint(sketch, "E289.visualSharp", {"position": v(-641.35, -889) * mm});
            skArc(sketch, "E289.filletArc", {"start": v(-641.35, -863.6) * mm, "mid": v(-633.91, -881.56) * mm, "end": v(-615.95, -889) * mm});
            skLineSegment(sketch, "E290", {"start": v(-333.38, -736.6) * mm, "end": v(-333.38, -889) * mm, "construction": true});
            skLineSegment(sketch, "E291", {"start": v(-641.35, -812.8) * mm, "end": v(-25.4, -812.8) * mm, "construction": true});
            skLineSegment(sketch, "E292", {"start": v(-384.18, -749.3) * mm, "end": v(-384.18, -755.65) * mm});
            skLineSegment(sketch, "E293", {"start": v(-377.83, -762) * mm, "end": v(-288.93, -762) * mm});
            skLineSegment(sketch, "E294", {"start": v(-282.58, -755.65) * mm, "end": v(-282.58, -749.3) * mm});
            skLineSegment(sketch, "E295.trimOffspring", {"start": v(-396.88, -736.6) * mm, "end": v(-615.95, -736.6) * mm});
            skPoint(sketch, "E296.visualSharp", {"position": v(-384.18, -736.6) * mm});
            skArc(sketch, "E296.filletArc", {"start": v(-384.18, -749.3) * mm, "mid": v(-387.9, -740.32) * mm, "end": v(-396.88, -736.6) * mm});
            skPoint(sketch, "E297.visualSharp", {"position": v(-282.58, -736.6) * mm});
            skArc(sketch, "E297.filletArc", {"start": v(-269.88, -736.6) * mm, "mid": v(-278.86, -740.32) * mm, "end": v(-282.57, -749.3) * mm});
            skPoint(sketch, "E298.visualSharp", {"position": v(-384.18, -762) * mm});
            skArc(sketch, "E298.filletArc", {"start": v(-384.18, -755.65) * mm, "mid": v(-382.32, -760.14) * mm, "end": v(-377.83, -762) * mm});
            skPoint(sketch, "E299.visualSharp", {"position": v(-282.58, -762) * mm});
            skArc(sketch, "E299.filletArc", {"start": v(-288.93, -762) * mm, "mid": v(-284.43, -760.14) * mm, "end": v(-282.58, -755.65) * mm});
            skLineSegment(sketch, "E300.MirrorCS", {"start": v(384.17, -749.3) * mm, "end": v(384.17, -755.65) * mm});
            skLineSegment(sketch, "E301.MirrorCS", {"start": v(282.57, -755.65) * mm, "end": v(282.57, -749.3) * mm});
            skArc(sketch, "E302.MirrorCS", {"start": v(288.92, -762) * mm, "mid": v(284.43, -760.14) * mm, "end": v(282.57, -755.65) * mm});
            skArc(sketch, "E303.MirrorCS", {"start": v(384.17, -755.65) * mm, "mid": v(382.32, -760.14) * mm, "end": v(377.82, -762) * mm});
            skArc(sketch, "E304.MirrorCS", {"start": v(269.87, -736.6) * mm, "mid": v(278.86, -740.32) * mm, "end": v(282.57, -749.3) * mm});
            skArc(sketch, "E305.MirrorCS", {"start": v(384.17, -749.3) * mm, "mid": v(387.9, -740.32) * mm, "end": v(396.87, -736.6) * mm});
            skLineSegment(sketch, "E306.MirrorCS", {"start": v(641.35, -762) * mm, "end": v(641.35, -863.6) * mm});
            skLineSegment(sketch, "E307.MirrorCS", {"start": v(396.87, -736.6) * mm, "end": v(615.95, -736.6) * mm});
            skPoint(sketch, "E308.MirrorP", {"position": v(25.4, -889) * mm});
            skLineSegment(sketch, "E309.MirrorCS", {"start": v(333.37, -736.6) * mm, "end": v(333.37, -889) * mm, "construction": true});
            skLineSegment(sketch, "E310.MirrorCS", {"start": v(641.35, -812.8) * mm, "end": v(25.4, -812.8) * mm, "construction": true});
            skLineSegment(sketch, "E311.MirrorCS", {"start": v(377.82, -762) * mm, "end": v(288.92, -762) * mm});
            skArc(sketch, "E312.MirrorCS", {"start": v(50.8, -889) * mm, "mid": v(32.84, -881.56) * mm, "end": v(25.4, -863.6) * mm});
            skPoint(sketch, "E313.MirrorP", {"position": v(282.57, -736.6) * mm});
            skPoint(sketch, "E314.MirrorP", {"position": v(641.35, -736.6) * mm});
            skPoint(sketch, "E315.MirrorP", {"position": v(384.17, -736.6) * mm});
            skPoint(sketch, "E316.MirrorP", {"position": v(282.57, -762) * mm});
            skPoint(sketch, "E317.MirrorP", {"position": v(641.35, -889) * mm});
            skLineSegment(sketch, "E318.MirrorCS", {"start": v(50.8, -736.6) * mm, "end": v(269.87, -736.6) * mm});
            skLineSegment(sketch, "E319.MirrorCS", {"start": v(50.8, -889) * mm, "end": v(615.95, -889) * mm});
            skLineSegment(sketch, "E320.MirrorCS", {"start": v(25.4, -863.6) * mm, "end": v(25.4, -762) * mm});
            skPoint(sketch, "E321.MirrorP", {"position": v(384.17, -762) * mm});
            skArc(sketch, "E322.MirrorCS", {"start": v(25.4, -762) * mm, "mid": v(32.84, -744.04) * mm, "end": v(50.8, -736.6) * mm});
            skArc(sketch, "E323.MirrorCS", {"start": v(615.95, -736.6) * mm, "mid": v(633.91, -744.04) * mm, "end": v(641.35, -762) * mm});
            skPoint(sketch, "E324.MirrorP", {"position": v(25.4, -736.6) * mm});
            skArc(sketch, "E325.MirrorCS", {"start": v(641.35, -863.6) * mm, "mid": v(633.91, -881.56) * mm, "end": v(615.95, -889) * mm});
            skSolve(sketch);
        }
        {
            var Q0;
            Q0 = qSketchRegion(id + "F27", true);
            extrude(context, id + "F28", {"entities" : qUnion([Q0]), "operationType" : NewBodyOperationType.ADD, "depth" : 19.05 * mm});
        }
    });
